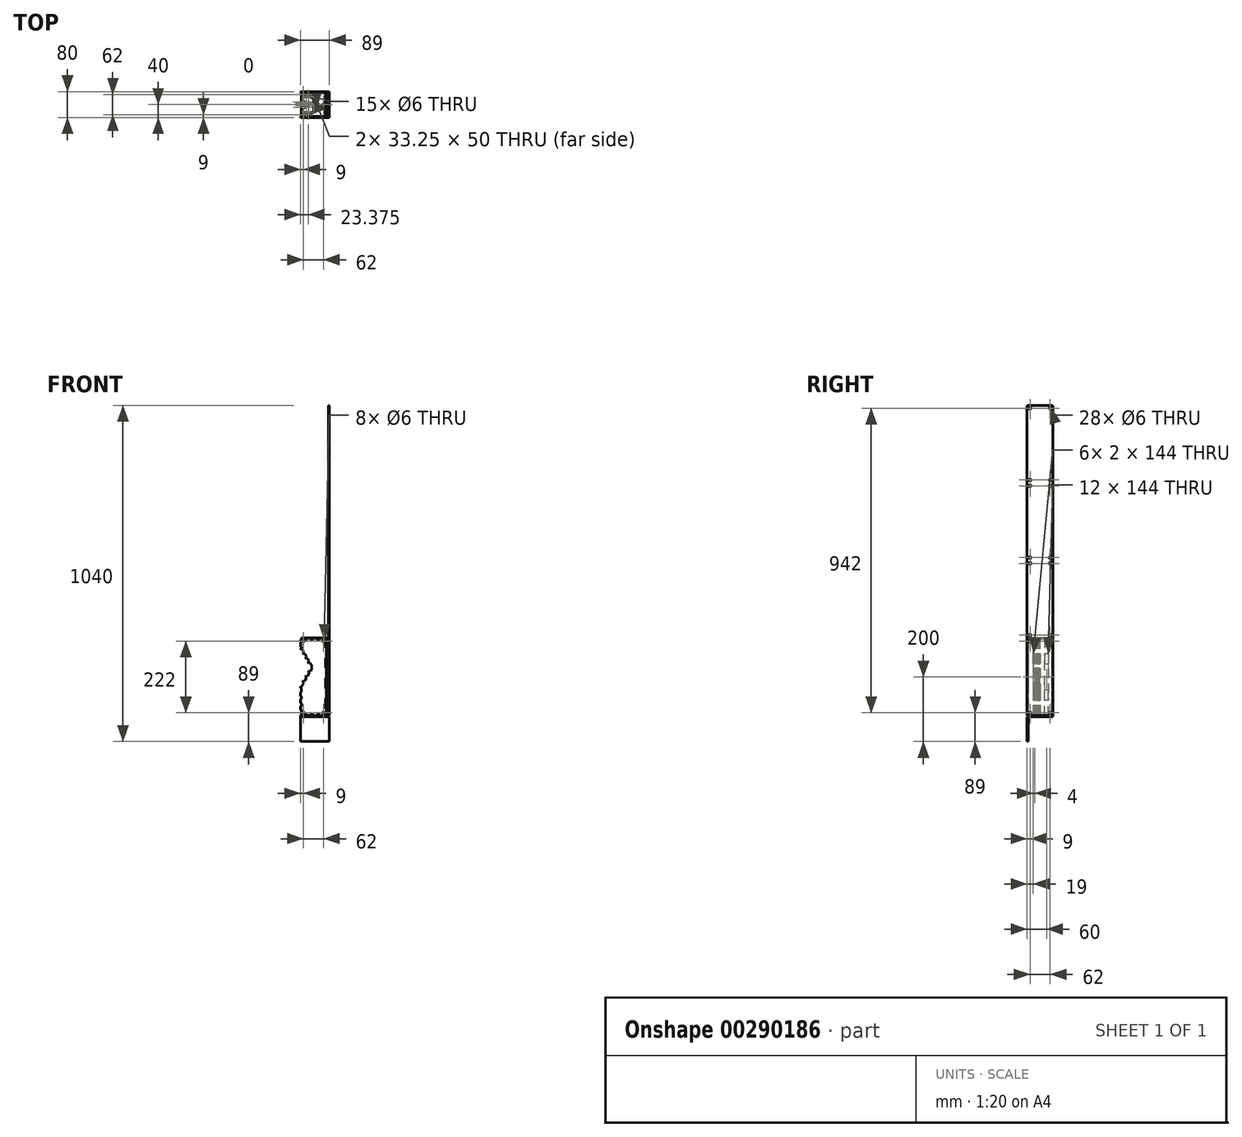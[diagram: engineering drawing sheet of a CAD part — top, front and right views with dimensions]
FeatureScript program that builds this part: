
annotation { "Feature Type Name" : "Feature", "Feature Type Description" : "" }
export const myFeature = defineFeature(function(context is Context, id is Id, definition is map)
    precondition{}
    {
        {
            assignVariable(context, id + "F0", {"name" : "WT", "anyValue" : 3});
        }
        {
            assignVariable(context, id + "F1", {"name" : "HD", "anyValue" : 3});
        }
        {
            var Q0;
            Q0=qCreatedBy(makeId("Front.planeOp"),FACE);
            var sketch = newSketch(context, id + "F2", { "sketchPlane" : qUnion([Q0])});
            skLineSegment(sketch, "E0", {"start": v(0, 0) * mm, "end": v(0, 240) * mm});
            skLineSegment(sketch, "E1", {"start": v(0, 120) * mm, "end": v(-80, 120) * mm, "construction": true});
            skLineSegment(sketch, "E2", {"start": v(0, 0) * mm, "end": v(-80, 0) * mm});
            skLineSegment(sketch, "E3", {"start": v(-80, 0) * mm, "end": v(-80, 90.56) * mm});
            skLineSegment(sketch, "E4", {"start": v(-80, 90.56) * mm, "end": v(-46, 149.44) * mm});
            skLineSegment(sketch, "E5", {"start": v(-46, 149.44) * mm, "end": v(-80, 208.33) * mm});
            skLineSegment(sketch, "E6", {"start": v(-80, 208.33) * mm, "end": v(-80, 240) * mm});
            skLineSegment(sketch, "E7", {"start": v(-80, 240) * mm, "end": v(0, 240) * mm});
            skLineSegment(sketch, "E8", {"start": v(-80, 90.56) * mm, "end": v(0, 90.56) * mm, "construction": true});
            skLineSegment(sketch, "E9", {"start": v(-80, 208.33) * mm, "end": v(0, 208.33) * mm, "construction": true});
            skPoint(sketch, "E10", {"position": v(-63, 120) * mm});
            skLineSegment(sketch, "E11", {"start": v(-80, 90.56) * mm, "end": v(-77, 90.56) * mm});
            skLineSegment(sketch, "E12", {"start": v(-77, 90.56) * mm, "end": v(-77, 0) * mm});
            skLineSegment(sketch, "E13", {"start": v(-3, 0) * mm, "end": v(-3, 240) * mm});
            skLineSegment(sketch, "E14", {"start": v(0, 237) * mm, "end": v(-80, 237) * mm});
            skLineSegment(sketch, "E15", {"start": v(-77, 240) * mm, "end": v(-77, 208.33) * mm});
            skLineSegment(sketch, "E16", {"start": v(-80, 208.33) * mm, "end": v(-77, 208.33) * mm});
            skLineSegment(sketch, "E17", {"start": v(-80, 3) * mm, "end": v(0, 3) * mm});
            skLineSegment(sketch, "E18", {"start": v(-80, 90.56) * mm, "end": v(-77.4, 89.06) * mm});
            skLineSegment(sketch, "E19", {"start": v(-77.4, 89.06) * mm, "end": v(-43.4, 147.94) * mm});
            skLineSegment(sketch, "E20", {"start": v(-80, 208.33) * mm, "end": v(-77.4, 209.83) * mm});
            skLineSegment(sketch, "E21", {"start": v(-77.4, 209.83) * mm, "end": v(-42.54, 149.44) * mm});
            skLineSegment(sketch, "E22", {"start": v(-46, 149.44) * mm, "end": v(-45.13, 147.94) * mm});
            skLineSegment(sketch, "E23", {"start": v(-45.13, 147.94) * mm, "end": v(-42.54, 149.44) * mm});
            skLineSegment(sketch, "E24", {"start": v(-43.4, 147.94) * mm, "end": v(-42.54, 149.44) * mm});
            skLineSegment(sketch, "E25", {"start": v(-46, 149.44) * mm, "end": v(-45.13, 150.94) * mm});
            skLineSegment(sketch, "E26", {"start": v(-45.13, 150.94) * mm, "end": v(-42.54, 149.44) * mm});
            skLineSegment(sketch, "E27", {"start": v(-76.65, 208.54) * mm, "end": v(-79.25, 207.04) * mm});
            skLineSegment(sketch, "E28", {"start": v(-46.43, 150.2) * mm, "end": v(-43.83, 151.7) * mm});
            skPoint(sketch, "E29", {"position": v(-79.25, 207.04) * mm});
            skPoint(sketch, "E30", {"position": v(-46.43, 150.2) * mm});
            skPoint(sketch, "E31", {"position": v(-80, 89.06) * mm});
            skCircle(sketch, "E32", {"center": v(-71, 231) * mm, "radius": 3 * mm});
            skLineSegment(sketch, "E33", {"start": v(-40, 208.33) * mm, "end": v(-40, 225.54) * mm, "construction": true});
            skCircle(sketch, "E34.MirrorC", {"center": v(-9, 231) * mm, "radius": 3 * mm});
            skCircle(sketch, "E35.MirrorC", {"center": v(-71, 9) * mm, "radius": 3 * mm});
            skCircle(sketch, "E36.MirrorC", {"center": v(-9, 9) * mm, "radius": 3 * mm});
            skSolve(sketch);
        }
        {
            var Q0;
            Q0=qCreatedBy(makeId("Front.planeOp"),FACE);
            var sketch = newSketch(context, id + "F3", { "sketchPlane" : qUnion([Q0])});
            skLineSegment(sketch, "E37.0", {"start": v(-80, 240) * mm, "end": v(0, 240) * mm});
            skLineSegment(sketch, "E37.1", {"start": v(-80, 208.33) * mm, "end": v(-80, 240) * mm});
            skLineSegment(sketch, "E37.2", {"start": v(-46, 149.44) * mm, "end": v(-80, 208.33) * mm});
            skLineSegment(sketch, "E37.3", {"start": v(-80, 90.56) * mm, "end": v(-46, 149.44) * mm});
            skLineSegment(sketch, "E37.4", {"start": v(-80, 0) * mm, "end": v(-80, 90.56) * mm});
            skLineSegment(sketch, "E37.5", {"start": v(0, 0) * mm, "end": v(-80, 0) * mm});
            skLineSegment(sketch, "E37.6", {"start": v(0, 0) * mm, "end": v(0, 240) * mm});
            skCircle(sketch, "E38.0", {"center": v(-71, 231) * mm, "radius": 3 * mm});
            skCircle(sketch, "E38.1", {"center": v(-9, 231) * mm, "radius": 3 * mm});
            skCircle(sketch, "E38.2", {"center": v(-71, 9) * mm, "radius": 3 * mm});
            skCircle(sketch, "E38.3", {"center": v(-9, 9) * mm, "radius": 3 * mm});
            skLineSegment(sketch, "E39", {"start": v(0, -80) * mm, "end": v(-80, -80) * mm});
            skLineSegment(sketch, "E40", {"start": v(-80, -80) * mm, "end": v(-80, 0) * mm});
            skLineSegment(sketch, "E41", {"start": v(0, 0) * mm, "end": v(9, 0) * mm});
            skLineSegment(sketch, "E42", {"start": v(9, 0) * mm, "end": v(9, -80) * mm});
            skLineSegment(sketch, "E43", {"start": v(9, -80) * mm, "end": v(0, -80) * mm});
            skSolve(sketch);
        }
        {
            var Q0;
            Q0=sQuery(id+"F2.wireOp",EDGE,"E7");
            cPlane(context, id + "F4", {"entities" : qUnion([Q0]), "cplaneType" : CPlaneType.LINE_ANGLE, "offset" : 25 * mm, "angle" : 90 * degree, "width" : 150 * mm, "height" : 150 * mm});
        }
        {
            var Q0;
            Q0=qCreatedBy(id+"F4.planeOp",FACE);
            var sketch = newSketch(context, id + "F5", { "sketchPlane" : qUnion([Q0])});
            skLineSegment(sketch, "E44.0", {"start": v(-80, 0) * mm, "end": v(0, 0) * mm});
            skLineSegment(sketch, "E45", {"start": v(-80, 0) * mm, "end": v(-80, 80) * mm});
            skLineSegment(sketch, "E46", {"start": v(-80, 80) * mm, "end": v(0, 80) * mm});
            skLineSegment(sketch, "E47", {"start": v(0, 80) * mm, "end": v(0, 0) * mm});
            skLineSegment(sketch, "E48", {"start": v(0, 40) * mm, "end": v(-80, 40) * mm, "construction": true});
            skLineSegment(sketch, "E49", {"start": v(-80, 77) * mm, "end": v(0, 77) * mm});
            skLineSegment(sketch, "E50", {"start": v(-70, 80) * mm, "end": v(-70, 77) * mm});
            skLineSegment(sketch, "E51.1.0.0", {"start": v(-60, 80) * mm, "end": v(-60, 77) * mm});
            skLineSegment(sketch, "E51.2.0.0", {"start": v(-50, 80) * mm, "end": v(-50, 77) * mm});
            skLineSegment(sketch, "E51.3.0.0", {"start": v(-40, 80) * mm, "end": v(-40, 77) * mm});
            skLineSegment(sketch, "E51.4.0.0", {"start": v(-30, 80) * mm, "end": v(-30, 77) * mm});
            skLineSegment(sketch, "E51.5.0.0", {"start": v(-20, 80) * mm, "end": v(-20, 77) * mm});
            skLineSegment(sketch, "E51.6.0.0", {"start": v(-10, 80) * mm, "end": v(-10, 77) * mm});
            skLineSegment(sketch, "E51.direction1", {"start": v(-70, 77) * mm, "end": v(-60, 77) * mm, "construction": true});
            skLineSegment(sketch, "E52.MirrorCS", {"start": v(-80, 3) * mm, "end": v(0, 3) * mm});
            skLineSegment(sketch, "E53.MirrorCS", {"start": v(-70, 0) * mm, "end": v(-70, 3) * mm});
            skLineSegment(sketch, "E54.MirrorCS", {"start": v(-60, 0) * mm, "end": v(-60, 3) * mm});
            skLineSegment(sketch, "E55.MirrorCS", {"start": v(-50, 0) * mm, "end": v(-50, 3) * mm});
            skLineSegment(sketch, "E56.MirrorCS", {"start": v(-40, 0) * mm, "end": v(-40, 3) * mm});
            skLineSegment(sketch, "E57.MirrorCS", {"start": v(-30, 0) * mm, "end": v(-30, 3) * mm});
            skLineSegment(sketch, "E58.MirrorCS", {"start": v(-20, 0) * mm, "end": v(-20, 3) * mm});
            skLineSegment(sketch, "E59.MirrorCS", {"start": v(-10, 0) * mm, "end": v(-10, 3) * mm});
            skLineSegment(sketch, "E60", {"start": v(-77, 80) * mm, "end": v(-77, 0) * mm});
            skLineSegment(sketch, "E61", {"start": v(-80, 71.1) * mm, "end": v(-77, 71.1) * mm});
            skLineSegment(sketch, "E62.0.1.0", {"start": v(-80, 62.34) * mm, "end": v(-77, 62.34) * mm});
            skLineSegment(sketch, "E62.0.2.0", {"start": v(-80, 53.6) * mm, "end": v(-77, 53.6) * mm});
            skLineSegment(sketch, "E62.0.3.0", {"start": v(-80, 44.84) * mm, "end": v(-77, 44.84) * mm});
            skLineSegment(sketch, "E62.0.4.0", {"start": v(-80, 36.1) * mm, "end": v(-77, 36.1) * mm});
            skLineSegment(sketch, "E62.0.5.0", {"start": v(-80, 27.34) * mm, "end": v(-77, 27.34) * mm});
            skLineSegment(sketch, "E62.0.6.0", {"start": v(-80, 18.6) * mm, "end": v(-77, 18.6) * mm});
            skLineSegment(sketch, "E62.direction1", {"start": v(-86.03, 71.1) * mm, "end": v(-80, 71.1) * mm, "construction": true});
            skLineSegment(sketch, "E62.direction2", {"start": v(-80, 71.1) * mm, "end": v(-80, 62.34) * mm, "construction": true});
            skLineSegment(sketch, "E63", {"start": v(-40, 40) * mm, "end": v(-40, 50.28) * mm, "construction": true});
            skLineSegment(sketch, "E64.MirrorCS", {"start": v(0, 18.6) * mm, "end": v(-3, 18.6) * mm});
            skLineSegment(sketch, "E65.MirrorCS", {"start": v(0, 27.34) * mm, "end": v(-3, 27.34) * mm});
            skLineSegment(sketch, "E66.MirrorCS", {"start": v(0, 36.1) * mm, "end": v(-3, 36.1) * mm});
            skLineSegment(sketch, "E67.MirrorCS", {"start": v(0, 44.84) * mm, "end": v(-3, 44.84) * mm});
            skLineSegment(sketch, "E68.MirrorCS", {"start": v(0, 53.6) * mm, "end": v(-3, 53.6) * mm});
            skLineSegment(sketch, "E69.MirrorCS", {"start": v(0, 62.34) * mm, "end": v(-3, 62.34) * mm});
            skLineSegment(sketch, "E70.MirrorCS", {"start": v(0, 71.1) * mm, "end": v(-3, 71.1) * mm});
            skLineSegment(sketch, "E71.MirrorCS", {"start": v(-3, 80) * mm, "end": v(-3, 0) * mm});
            skLineSegment(sketch, "E72.bottom", {"start": v(-40, 15) * mm, "end": v(-73.25, 15) * mm});
            skLineSegment(sketch, "E72.top", {"start": v(-40, 65) * mm, "end": v(-73.25, 65) * mm});
            skLineSegment(sketch, "E72.left", {"start": v(-6.75, 40) * mm, "end": v(-6.75, 65) * mm, "construction": true});
            skLineSegment(sketch, "E72.right", {"start": v(-73.25, 15) * mm, "end": v(-73.25, 65) * mm});
            skPoint(sketch, "E72.middle", {"position": v(-40, 40) * mm});
            skCircle(sketch, "E73", {"center": v(-9, 40) * mm, "radius": 3 * mm});
            skCircle(sketch, "E74.MirrorC", {"center": v(-71, 71) * mm, "radius": 3 * mm});
            skLineSegment(sketch, "E75", {"start": v(-40, 15) * mm, "end": v(-40, 65) * mm});
            skPoint(sketch, "E76.orphan", {"position": v(-6.75, 15) * mm});
            skCircle(sketch, "E77.MirrorC", {"center": v(-71, 9) * mm, "radius": 3 * mm});
            skLineSegment(sketch, "E78.0.0.7", {"start": v(-80, 9.84) * mm, "end": v(-77, 9.84) * mm});
            skLineSegment(sketch, "E79.MirrorCS", {"start": v(0, 9.84) * mm, "end": v(-3, 9.84) * mm});
            skSolve(sketch);
        }
        {
            var Q0;
            Q0=sQuery(id+"F2.wireOp",EDGE,"E0");
            cPlane(context, id + "F6", {"entities" : qUnion([Q0]), "cplaneType" : CPlaneType.LINE_ANGLE, "offset" : 25 * mm, "angle" : 0 * degree, "width" : 150 * mm, "height" : 150 * mm});
        }
        {
            var Q0;
            Q0=qCreatedBy(id+"F6.planeOp",FACE);
            var sketch = newSketch(context, id + "F7", { "sketchPlane" : qUnion([Q0])});
            skLineSegment(sketch, "E80.0", {"start": v(0, 0) * mm, "end": v(0, 240) * mm});
            skLineSegment(sketch, "E81.0", {"start": v(80, 240) * mm, "end": v(0, 240) * mm});
            skLineSegment(sketch, "E82", {"start": v(80, 240) * mm, "end": v(80, 0) * mm});
            skLineSegment(sketch, "E83", {"start": v(80, 0) * mm, "end": v(0, 0) * mm});
            skLineSegment(sketch, "E84", {"start": v(3, 240) * mm, "end": v(3, 0) * mm});
            skLineSegment(sketch, "E85", {"start": v(0, 210) * mm, "end": v(3, 210) * mm});
            skLineSegment(sketch, "E86.0.1.0", {"start": v(0, 178.75) * mm, "end": v(3, 178.75) * mm});
            skLineSegment(sketch, "E86.0.2.0", {"start": v(0, 147.5) * mm, "end": v(3, 147.5) * mm});
            skLineSegment(sketch, "E86.0.3.0", {"start": v(0, 116.25) * mm, "end": v(3, 116.25) * mm});
            skLineSegment(sketch, "E86.0.4.0", {"start": v(0, 85) * mm, "end": v(3, 85) * mm});
            skLineSegment(sketch, "E86.0.5.0", {"start": v(0, 53.75) * mm, "end": v(3, 53.75) * mm});
            skLineSegment(sketch, "E86.0.6.0", {"start": v(0, 22.5) * mm, "end": v(3, 22.5) * mm});
            skLineSegment(sketch, "E86.direction1", {"start": v(-5.68, 210) * mm, "end": v(0, 210) * mm, "construction": true});
            skLineSegment(sketch, "E86.direction2", {"start": v(0, 210) * mm, "end": v(0, 178.75) * mm, "construction": true});
            skLineSegment(sketch, "E87", {"start": v(40, 240) * mm, "end": v(40, 220.49) * mm, "construction": true});
            skPoint(sketch, "E87.endSnap0", {"position": v(40, 240) * mm});
            skLineSegment(sketch, "E88.MirrorCS", {"start": v(77, 240) * mm, "end": v(77, 0) * mm});
            skLineSegment(sketch, "E89.MirrorCS", {"start": v(80, 210) * mm, "end": v(77, 210) * mm});
            skLineSegment(sketch, "E90.MirrorCS", {"start": v(80, 178.75) * mm, "end": v(77, 178.75) * mm});
            skLineSegment(sketch, "E91.MirrorCS", {"start": v(80, 147.5) * mm, "end": v(77, 147.5) * mm});
            skLineSegment(sketch, "E92.MirrorCS", {"start": v(80, 116.25) * mm, "end": v(77, 116.25) * mm});
            skLineSegment(sketch, "E93.MirrorCS", {"start": v(80, 85) * mm, "end": v(77, 85) * mm});
            skLineSegment(sketch, "E94.MirrorCS", {"start": v(80, 53.75) * mm, "end": v(77, 53.75) * mm});
            skLineSegment(sketch, "E95.MirrorCS", {"start": v(80, 22.5) * mm, "end": v(77, 22.5) * mm});
            skCircle(sketch, "E96", {"center": v(9, 231) * mm, "radius": 3 * mm});
            skCircle(sketch, "E97.MirrorC", {"center": v(71, 231) * mm, "radius": 3 * mm});
            skLineSegment(sketch, "E98", {"start": v(77, 120) * mm, "end": v(3, 120) * mm, "construction": true});
            skCircle(sketch, "E99.MirrorC", {"center": v(9, 9) * mm, "radius": 3 * mm});
            skCircle(sketch, "E100.MirrorC", {"center": v(71, 9) * mm, "radius": 3 * mm});
            skSolve(sketch);
        }
        {
            var Q0;
            Q0=sQuery(id+"F2.wireOp",EDGE,"E2");
            cPlane(context, id + "F8", {"entities" : qUnion([Q0]), "cplaneType" : CPlaneType.LINE_ANGLE, "offset" : 25 * mm, "angle" : 90 * degree, "width" : 150 * mm, "height" : 150 * mm});
        }
        {
            var Q0;
            Q0=qCreatedBy(id+"F8.planeOp",FACE);
            var sketch = newSketch(context, id + "F9", { "sketchPlane" : qUnion([Q0])});
            skLineSegment(sketch, "E101.0", {"start": v(-80, 0) * mm, "end": v(0, 0) * mm});
            skLineSegment(sketch, "E101.1", {"start": v(0, 80) * mm, "end": v(0, 0) * mm});
            skLineSegment(sketch, "E101.2", {"start": v(-80, 0) * mm, "end": v(-80, 80) * mm});
            skLineSegment(sketch, "E101.3", {"start": v(-80, 80) * mm, "end": v(0, 80) * mm});
            skLineSegment(sketch, "E101.4", {"start": v(-80, 77) * mm, "end": v(0, 77) * mm});
            skLineSegment(sketch, "E101.5", {"start": v(-3, 80) * mm, "end": v(-3, 0) * mm});
            skLineSegment(sketch, "E101.6", {"start": v(-77, 80) * mm, "end": v(-77, 0) * mm});
            skLineSegment(sketch, "E101.7", {"start": v(-70, 80) * mm, "end": v(-70, 77) * mm});
            skLineSegment(sketch, "E101.8", {"start": v(-60, 80) * mm, "end": v(-60, 77) * mm});
            skLineSegment(sketch, "E101.9", {"start": v(-50, 80) * mm, "end": v(-50, 77) * mm});
            skLineSegment(sketch, "E101.10", {"start": v(-40, 80) * mm, "end": v(-40, 77) * mm});
            skLineSegment(sketch, "E101.11", {"start": v(-30, 80) * mm, "end": v(-30, 77) * mm});
            skLineSegment(sketch, "E101.12", {"start": v(-20, 80) * mm, "end": v(-20, 77) * mm});
            skLineSegment(sketch, "E101.13", {"start": v(-10, 80) * mm, "end": v(-10, 77) * mm});
            skLineSegment(sketch, "E101.14", {"start": v(0, 71.1) * mm, "end": v(-3, 71.1) * mm});
            skLineSegment(sketch, "E101.15", {"start": v(0, 62.34) * mm, "end": v(-3, 62.34) * mm});
            skLineSegment(sketch, "E101.16", {"start": v(0, 53.6) * mm, "end": v(-3, 53.6) * mm});
            skLineSegment(sketch, "E101.17", {"start": v(0, 36.1) * mm, "end": v(-3, 36.1) * mm});
            skLineSegment(sketch, "E101.18", {"start": v(0, 27.34) * mm, "end": v(-3, 27.34) * mm});
            skLineSegment(sketch, "E101.19", {"start": v(0, 18.6) * mm, "end": v(-3, 18.6) * mm});
            skLineSegment(sketch, "E101.20", {"start": v(-80, 3) * mm, "end": v(0, 3) * mm});
            skLineSegment(sketch, "E101.21", {"start": v(-10, 0) * mm, "end": v(-10, 3) * mm});
            skLineSegment(sketch, "E101.22", {"start": v(-20, 0) * mm, "end": v(-20, 3) * mm});
            skLineSegment(sketch, "E101.23", {"start": v(-30, 0) * mm, "end": v(-30, 3) * mm});
            skLineSegment(sketch, "E101.24", {"start": v(-40, 0) * mm, "end": v(-40, 3) * mm});
            skLineSegment(sketch, "E101.25", {"start": v(-50, 0) * mm, "end": v(-50, 3) * mm});
            skLineSegment(sketch, "E101.26", {"start": v(-60, 0) * mm, "end": v(-60, 3) * mm});
            skLineSegment(sketch, "E101.27", {"start": v(-70, 0) * mm, "end": v(-70, 3) * mm});
            skLineSegment(sketch, "E101.28", {"start": v(-80, 18.6) * mm, "end": v(-77, 18.6) * mm});
            skLineSegment(sketch, "E101.29", {"start": v(-80, 27.34) * mm, "end": v(-77, 27.34) * mm});
            skLineSegment(sketch, "E101.30", {"start": v(-80, 36.1) * mm, "end": v(-77, 36.1) * mm});
            skLineSegment(sketch, "E101.31", {"start": v(-80, 44.84) * mm, "end": v(-77, 44.84) * mm});
            skLineSegment(sketch, "E101.32", {"start": v(-80, 53.6) * mm, "end": v(-77, 53.6) * mm});
            skLineSegment(sketch, "E101.33", {"start": v(-80, 62.34) * mm, "end": v(-77, 62.34) * mm});
            skLineSegment(sketch, "E101.34", {"start": v(-80, 71.1) * mm, "end": v(-77, 71.1) * mm});
            skLineSegment(sketch, "E101.35", {"start": v(0, 44.84) * mm, "end": v(-3, 44.84) * mm});
            skCircle(sketch, "E102.0", {"center": v(-71, 71) * mm, "radius": 3 * mm});
            skCircle(sketch, "E102.2", {"center": v(-9, 40) * mm, "radius": 3 * mm});
            skLineSegment(sketch, "E103.0", {"start": v(-6.75, 40) * mm, "end": v(-6.75, 65) * mm});
            skLineSegment(sketch, "E104", {"start": v(-6.75, 52.5) * mm, "end": v(-34.86, 52.5) * mm, "construction": true});
            skLineSegment(sketch, "E105.0", {"start": v(-73.25, 15) * mm, "end": v(-73.25, 65) * mm});
            skLineSegment(sketch, "E106", {"start": v(-73.25, 40) * mm, "end": v(-49.8, 40) * mm, "construction": true});
            skPoint(sketch, "E106.endSnap0", {"position": v(-73.25, 40) * mm});
            skCircle(sketch, "E107", {"center": v(-70.25, 40) * mm, "radius": 3 * mm});
            skLineSegment(sketch, "E108", {"start": v(-70.25, 40) * mm, "end": v(-70.25, 48) * mm, "construction": true});
            skCircle(sketch, "E109", {"center": v(-70.25, 48) * mm, "radius": 3 * mm});
            skCircle(sketch, "E110.MirrorC", {"center": v(-70.25, 32) * mm, "radius": 3 * mm});
            skLineSegment(sketch, "E111", {"start": v(-70.25, 44) * mm, "end": v(-62.25, 44) * mm, "construction": true});
            skCircle(sketch, "E112", {"center": v(-62.25, 44) * mm, "radius": 3 * mm});
            skCircle(sketch, "E113.MirrorC", {"center": v(-62.25, 36) * mm, "radius": 3 * mm});
            skLineSegment(sketch, "E114", {"start": v(-62.25, 44) * mm, "end": v(-62.25, 31.93) * mm, "construction": true});
            skCircle(sketch, "E115.MirrorC", {"center": v(-54.25, 40) * mm, "radius": 3 * mm});
            skCircle(sketch, "E116.0", {"center": v(-71, 9) * mm, "radius": 3 * mm});
            skSolve(sketch);
        }
        {
            var Q0;
            Q0=sQuery(id+"F7.wireOp",EDGE,"E82");
            cPlane(context, id + "F10", {"entities" : qUnion([Q0]), "cplaneType" : CPlaneType.LINE_ANGLE, "offset" : 25 * mm, "angle" : 90 * degree, "width" : 150 * mm, "height" : 150 * mm});
        }
        {
            var Q0;
            Q0=qCreatedBy(id+"F10.planeOp",FACE);
            var sketch = newSketch(context, id + "F11", { "sketchPlane" : qUnion([Q0])});
            skLineSegment(sketch, "E117.0", {"start": v(80, 208.33) * mm, "end": v(80, 240) * mm});
            skLineSegment(sketch, "E117.1", {"start": v(46, 149.44) * mm, "end": v(80, 208.33) * mm});
            skLineSegment(sketch, "E117.2", {"start": v(80, 90.56) * mm, "end": v(46, 149.44) * mm});
            skLineSegment(sketch, "E117.3", {"start": v(80, 0) * mm, "end": v(80, 90.56) * mm});
            skLineSegment(sketch, "E117.4", {"start": v(0, 0) * mm, "end": v(80, 0) * mm});
            skLineSegment(sketch, "E117.5", {"start": v(0, 0) * mm, "end": v(0, 240) * mm});
            skLineSegment(sketch, "E117.6", {"start": v(80, 240) * mm, "end": v(0, 240) * mm});
            skCircle(sketch, "E118", {"center": v(9, 231) * mm, "radius": 3 * mm});
            skLineSegment(sketch, "E119", {"start": v(40, 240) * mm, "end": v(40, 223.94) * mm, "construction": true});
            skCircle(sketch, "E120.MirrorC", {"center": v(71, 231) * mm, "radius": 3 * mm});
            skCircle(sketch, "E121.MirrorC", {"center": v(9, 9) * mm, "radius": 3 * mm});
            skCircle(sketch, "E122.MirrorC", {"center": v(71, 9) * mm, "radius": 3 * mm});
            skSolve(sketch);
        }
        {
            var Q0;
            Q0=sQuery(id+"F2.wireOp",EDGE,"E6");
            cPlane(context, id + "F12", {"entities" : qUnion([Q0]), "cplaneType" : CPlaneType.LINE_ANGLE, "offset" : 25 * mm, "angle" : 0 * degree, "width" : 150 * mm, "height" : 150 * mm});
        }
        {
            var Q0;
            Q0=qCreatedBy(id+"F12.planeOp",FACE);
            var sketch = newSketch(context, id + "F13", { "sketchPlane" : qUnion([Q0])});
            skLineSegment(sketch, "E123.0", {"start": v(0, 208.33) * mm, "end": v(0, 240) * mm});
            skLineSegment(sketch, "E124.0", {"start": v(0, 240) * mm, "end": v(80, 240) * mm});
            skLineSegment(sketch, "E125", {"start": v(80, 240) * mm, "end": v(80, 208.33) * mm});
            skLineSegment(sketch, "E126", {"start": v(80, 208.33) * mm, "end": v(0, 208.33) * mm});
            skLineSegment(sketch, "E127", {"start": v(80, 224.17) * mm, "end": v(0, 224.17) * mm, "construction": true});
            skLineSegment(sketch, "E128", {"start": v(80, 226.57) * mm, "end": v(77, 226.57) * mm});
            skLineSegment(sketch, "E129", {"start": v(77, 226.57) * mm, "end": v(77, 224.17) * mm});
            skLineSegment(sketch, "E130.MirrorCS", {"start": v(77, 221.77) * mm, "end": v(77, 224.17) * mm});
            skLineSegment(sketch, "E131.MirrorCS", {"start": v(80, 221.77) * mm, "end": v(77, 221.77) * mm});
            skLineSegment(sketch, "E132", {"start": v(80, 240) * mm, "end": v(0, 224.17) * mm, "construction": true});
            skLineSegment(sketch, "E133", {"start": v(40, 232.08) * mm, "end": v(80, 232.08) * mm, "construction": true});
            skLineSegment(sketch, "E134", {"start": v(80, 234.48) * mm, "end": v(77, 234.48) * mm});
            skLineSegment(sketch, "E135", {"start": v(77, 234.48) * mm, "end": v(77, 232.08) * mm});
            skLineSegment(sketch, "E136.MirrorCS", {"start": v(77, 229.68) * mm, "end": v(77, 232.08) * mm});
            skLineSegment(sketch, "E137.MirrorCS", {"start": v(80, 229.68) * mm, "end": v(77, 229.68) * mm});
            skLineSegment(sketch, "E138.MirrorCS", {"start": v(80, 218.65) * mm, "end": v(77, 218.65) * mm});
            skLineSegment(sketch, "E139.MirrorCS", {"start": v(77, 218.65) * mm, "end": v(77, 216.25) * mm});
            skLineSegment(sketch, "E140.MirrorCS", {"start": v(77, 213.85) * mm, "end": v(77, 216.25) * mm});
            skLineSegment(sketch, "E141.MirrorCS", {"start": v(80, 213.85) * mm, "end": v(77, 213.85) * mm});
            skLineSegment(sketch, "E142", {"start": v(40, 224.17) * mm, "end": v(40, 240) * mm, "construction": true});
            skLineSegment(sketch, "E143.MirrorCS", {"start": v(0, 234.48) * mm, "end": v(3, 234.48) * mm});
            skLineSegment(sketch, "E144.MirrorCS", {"start": v(3, 234.48) * mm, "end": v(3, 232.08) * mm});
            skLineSegment(sketch, "E145.MirrorCS", {"start": v(3, 229.68) * mm, "end": v(3, 232.08) * mm});
            skLineSegment(sketch, "E146.MirrorCS", {"start": v(0, 229.68) * mm, "end": v(3, 229.68) * mm});
            skLineSegment(sketch, "E147.MirrorCS", {"start": v(0, 226.57) * mm, "end": v(3, 226.57) * mm});
            skLineSegment(sketch, "E148.MirrorCS", {"start": v(3, 226.57) * mm, "end": v(3, 224.17) * mm});
            skLineSegment(sketch, "E149.MirrorCS", {"start": v(3, 221.77) * mm, "end": v(3, 224.17) * mm});
            skLineSegment(sketch, "E150.MirrorCS", {"start": v(0, 221.77) * mm, "end": v(3, 221.77) * mm});
            skLineSegment(sketch, "E151.MirrorCS", {"start": v(0, 218.65) * mm, "end": v(3, 218.65) * mm});
            skLineSegment(sketch, "E152.MirrorCS", {"start": v(3, 218.65) * mm, "end": v(3, 216.25) * mm});
            skLineSegment(sketch, "E153.MirrorCS", {"start": v(3, 213.85) * mm, "end": v(3, 216.25) * mm});
            skLineSegment(sketch, "E154.MirrorCS", {"start": v(0, 213.85) * mm, "end": v(3, 213.85) * mm});
            skSolve(sketch);
        }
        {
            var Q0;
            Q0=sQuery(id+"F11.wireOp",EDGE,"E117.3");
            cPlane(context, id + "F14", {"entities" : qUnion([Q0]), "cplaneType" : CPlaneType.LINE_ANGLE, "offset" : 25 * mm, "angle" : 0 * degree, "width" : 150 * mm, "height" : 150 * mm});
        }
        {
            var Q0;
            Q0=qCreatedBy(id+"F14.planeOp",FACE);
            var sketch = newSketch(context, id + "F15", { "sketchPlane" : qUnion([Q0])});
            skLineSegment(sketch, "E155.0", {"start": v(80, 0) * mm, "end": v(80, 90.56) * mm});
            skLineSegment(sketch, "E156.0", {"start": v(0, 0) * mm, "end": v(80, 0) * mm});
            skLineSegment(sketch, "E157", {"start": v(80, 89.06) * mm, "end": v(0, 89.06) * mm});
            skLineSegment(sketch, "E158", {"start": v(0, 89.06) * mm, "end": v(0, 0) * mm});
            skLineSegment(sketch, "E159", {"start": v(80, 45.28) * mm, "end": v(0, 44.53) * mm, "construction": true});
            skLineSegment(sketch, "E160", {"start": v(0, 44.53) * mm, "end": v(80, 89.06) * mm, "construction": true});
            skLineSegment(sketch, "E161", {"start": v(80, 51.28) * mm, "end": v(77, 51.25) * mm});
            skLineSegment(sketch, "E162", {"start": v(77, 51.25) * mm, "end": v(77, 45.25) * mm});
            skLineSegment(sketch, "E163.MirrorCS", {"start": v(77.11, 39.25) * mm, "end": v(77, 45.25) * mm});
            skLineSegment(sketch, "E164.MirrorCS", {"start": v(80.11, 39.28) * mm, "end": v(77.11, 39.25) * mm});
            skLineSegment(sketch, "E165", {"start": v(40, 66.8) * mm, "end": v(80, 66.8) * mm, "construction": true});
            skLineSegment(sketch, "E166", {"start": v(80, 72.8) * mm, "end": v(77, 72.8) * mm});
            skLineSegment(sketch, "E167", {"start": v(77, 72.8) * mm, "end": v(77, 66.8) * mm});
            skLineSegment(sketch, "E168.MirrorCS", {"start": v(77, 60.8) * mm, "end": v(77, 66.8) * mm});
            skLineSegment(sketch, "E169.MirrorCS", {"start": v(80, 60.8) * mm, "end": v(77, 60.8) * mm});
            skLineSegment(sketch, "E170.MirrorCS", {"start": v(80.3, 29.77) * mm, "end": v(77.3, 29.71) * mm});
            skLineSegment(sketch, "E171.MirrorCS", {"start": v(77.3, 29.71) * mm, "end": v(77.4, 23.71) * mm});
            skLineSegment(sketch, "E172.MirrorCS", {"start": v(77.52, 17.71) * mm, "end": v(77.4, 23.71) * mm});
            skLineSegment(sketch, "E173.MirrorCS", {"start": v(80.52, 17.77) * mm, "end": v(77.52, 17.71) * mm});
            skLineSegment(sketch, "E174", {"start": v(40, 66.8) * mm, "end": v(40, 35.43) * mm, "construction": true});
            skPoint(sketch, "E174.endSnap0", {"position": v(40, 44.9) * mm});
            skLineSegment(sketch, "E175.MirrorCS", {"start": v(0, 72.8) * mm, "end": v(3, 72.8) * mm});
            skLineSegment(sketch, "E176.MirrorCS", {"start": v(3, 72.8) * mm, "end": v(3, 66.8) * mm});
            skLineSegment(sketch, "E177.MirrorCS", {"start": v(3, 60.8) * mm, "end": v(3, 66.8) * mm});
            skLineSegment(sketch, "E178.MirrorCS", {"start": v(0, 60.8) * mm, "end": v(3, 60.8) * mm});
            skLineSegment(sketch, "E179.MirrorCS", {"start": v(0, 51.28) * mm, "end": v(3, 51.25) * mm});
            skLineSegment(sketch, "E180.MirrorCS", {"start": v(3, 51.25) * mm, "end": v(3, 45.25) * mm});
            skLineSegment(sketch, "E181.MirrorCS", {"start": v(2.89, 39.25) * mm, "end": v(3, 45.25) * mm});
            skLineSegment(sketch, "E182.MirrorCS", {"start": v(-0.11, 39.28) * mm, "end": v(2.89, 39.25) * mm});
            skLineSegment(sketch, "E183.MirrorCS", {"start": v(-0.3, 29.77) * mm, "end": v(2.7, 29.71) * mm});
            skLineSegment(sketch, "E184.MirrorCS", {"start": v(2.7, 29.71) * mm, "end": v(2.6, 23.71) * mm});
            skLineSegment(sketch, "E185.MirrorCS", {"start": v(2.48, 17.71) * mm, "end": v(2.6, 23.71) * mm});
            skLineSegment(sketch, "E186.MirrorCS", {"start": v(-0.52, 17.77) * mm, "end": v(2.48, 17.71) * mm});
            skPoint(sketch, "E187", {"position": v(80, 89.06) * mm});
            skLineSegment(sketch, "E188", {"start": v(0, 85.3) * mm, "end": v(3, 85.3) * mm});
            skLineSegment(sketch, "E189", {"start": v(3, 85.3) * mm, "end": v(3, 89.06) * mm});
            skLineSegment(sketch, "E190.MirrorCS", {"start": v(80, 85.3) * mm, "end": v(77, 85.3) * mm});
            skLineSegment(sketch, "E191.MirrorCS", {"start": v(77, 85.3) * mm, "end": v(77, 89.06) * mm});
            skSolve(sketch);
        }
        {
            var Q0;
            Q0=sQuery(id+"F2.wireOp",EDGE,"E5");
            cPlane(context, id + "F16", {"entities" : qUnion([Q0]), "cplaneType" : CPlaneType.LINE_ANGLE, "offset" : 25 * mm, "angle" : 0 * degree, "width" : 150 * mm, "height" : 150 * mm});
        }
        {
            var Q0;
            Q0=qCreatedBy(id+"F16.planeOp",FACE);
            var sketch = newSketch(context, id + "F17", { "sketchPlane" : qUnion([Q0])});
            skLineSegment(sketch, "E192.0", {"start": v(0, 152.42) * mm, "end": v(0, 220.42) * mm});
            skLineSegment(sketch, "E193", {"start": v(0, 153.29) * mm, "end": v(80, 153.29) * mm});
            skLineSegment(sketch, "E194", {"start": v(0, 218.92) * mm, "end": v(80, 218.92) * mm});
            skLineSegment(sketch, "E195", {"start": v(80, 218.92) * mm, "end": v(80, 153.29) * mm});
            skLineSegment(sketch, "E196", {"start": v(0, 186.42) * mm, "end": v(80, 186.42) * mm, "construction": true});
            skLineSegment(sketch, "E197", {"start": v(80, 186.42) * mm, "end": v(0, 218.92) * mm, "construction": true});
            skLineSegment(sketch, "E198", {"start": v(40, 202.67) * mm, "end": v(0, 202.67) * mm, "construction": true});
            skLineSegment(sketch, "E199", {"start": v(0, 190.17) * mm, "end": v(3, 190.17) * mm});
            skLineSegment(sketch, "E200", {"start": v(3, 190.17) * mm, "end": v(3, 186.42) * mm});
            skLineSegment(sketch, "E201.MirrorCS", {"start": v(3, 182.67) * mm, "end": v(3, 186.42) * mm});
            skLineSegment(sketch, "E202.MirrorCS", {"start": v(0, 182.67) * mm, "end": v(3, 182.67) * mm});
            skLineSegment(sketch, "E203", {"start": v(0, 206.42) * mm, "end": v(3, 206.42) * mm});
            skLineSegment(sketch, "E204", {"start": v(3, 206.42) * mm, "end": v(3, 202.67) * mm});
            skLineSegment(sketch, "E205.MirrorCS", {"start": v(3, 198.92) * mm, "end": v(3, 202.67) * mm});
            skLineSegment(sketch, "E206.MirrorCS", {"start": v(0, 198.92) * mm, "end": v(3, 198.92) * mm});
            skLineSegment(sketch, "E207.MirrorCS", {"start": v(3, 173.92) * mm, "end": v(3, 170.17) * mm});
            skLineSegment(sketch, "E208.MirrorCS", {"start": v(0, 173.92) * mm, "end": v(3, 173.92) * mm});
            skLineSegment(sketch, "E209.MirrorCS", {"start": v(3, 166.42) * mm, "end": v(3, 170.17) * mm});
            skLineSegment(sketch, "E210.MirrorCS", {"start": v(0, 166.42) * mm, "end": v(3, 166.42) * mm});
            skLineSegment(sketch, "E211", {"start": v(40, 202.67) * mm, "end": v(40, 174.67) * mm, "construction": true});
            skPoint(sketch, "E211.endSnap0", {"position": v(40, 186.42) * mm});
            skLineSegment(sketch, "E212.MirrorCS", {"start": v(80, 206.42) * mm, "end": v(77, 206.42) * mm});
            skLineSegment(sketch, "E213.MirrorCS", {"start": v(77, 206.42) * mm, "end": v(77, 202.67) * mm});
            skLineSegment(sketch, "E214.MirrorCS", {"start": v(77, 198.92) * mm, "end": v(77, 202.67) * mm});
            skLineSegment(sketch, "E215.MirrorCS", {"start": v(80, 198.92) * mm, "end": v(77, 198.92) * mm});
            skLineSegment(sketch, "E216.MirrorCS", {"start": v(80, 190.17) * mm, "end": v(77, 190.17) * mm});
            skLineSegment(sketch, "E217.MirrorCS", {"start": v(77, 190.17) * mm, "end": v(77, 186.42) * mm});
            skLineSegment(sketch, "E218.MirrorCS", {"start": v(77, 182.67) * mm, "end": v(77, 186.42) * mm});
            skLineSegment(sketch, "E219.MirrorCS", {"start": v(80, 182.67) * mm, "end": v(77, 182.67) * mm});
            skLineSegment(sketch, "E220.MirrorCS", {"start": v(80, 173.92) * mm, "end": v(77, 173.92) * mm});
            skLineSegment(sketch, "E221.MirrorCS", {"start": v(77, 173.92) * mm, "end": v(77, 170.17) * mm});
            skLineSegment(sketch, "E222.MirrorCS", {"start": v(77, 166.42) * mm, "end": v(77, 170.17) * mm});
            skLineSegment(sketch, "E223.MirrorCS", {"start": v(80, 166.42) * mm, "end": v(77, 166.42) * mm});
            skLineSegment(sketch, "E224", {"start": v(0, 215.17) * mm, "end": v(3, 215.17) * mm});
            skLineSegment(sketch, "E225", {"start": v(3, 215.17) * mm, "end": v(3, 218.92) * mm});
            skLineSegment(sketch, "E226.MirrorCS", {"start": v(77, 215.17) * mm, "end": v(77, 218.92) * mm});
            skLineSegment(sketch, "E227.MirrorCS", {"start": v(80, 215.17) * mm, "end": v(77, 215.17) * mm});
            skSolve(sketch);
        }
        {
            var Q0;
            Q0=sQuery(id+"F2.wireOp",EDGE,"E4");
            cPlane(context, id + "F18", {"entities" : qUnion([Q0]), "cplaneType" : CPlaneType.LINE_ANGLE, "offset" : 25 * mm, "angle" : 0 * degree, "width" : 150 * mm, "height" : 150 * mm});
        }
        {
            var Q0;
            Q0=qCreatedBy(id+"F18.planeOp",FACE);
            var sketch = newSketch(context, id + "F19", { "sketchPlane" : qUnion([Q0])});
            skLineSegment(sketch, "E228.0", {"start": v(0, 38.42) * mm, "end": v(0, 106.42) * mm});
            skLineSegment(sketch, "E228.1", {"start": v(0, 106.42) * mm, "end": v(0, 108.16) * mm});
            skLineSegment(sketch, "E229", {"start": v(0, 38.42) * mm, "end": v(80, 38.42) * mm});
            skLineSegment(sketch, "E230", {"start": v(80, 38.42) * mm, "end": v(80, 108.16) * mm});
            skLineSegment(sketch, "E231", {"start": v(80, 108.16) * mm, "end": v(0, 108.16) * mm});
            skLineSegment(sketch, "E232", {"start": v(80, 73.29) * mm, "end": v(0, 73.29) * mm, "construction": true});
            skLineSegment(sketch, "E233", {"start": v(0, 73.29) * mm, "end": v(80, 108.16) * mm, "construction": true});
            skLineSegment(sketch, "E234", {"start": v(40, 90.72) * mm, "end": v(0, 90.72) * mm, "construction": true});
            skLineSegment(sketch, "E235", {"start": v(0, 69.54) * mm, "end": v(3, 69.54) * mm});
            skLineSegment(sketch, "E236", {"start": v(3, 69.54) * mm, "end": v(3, 73.29) * mm});
            skLineSegment(sketch, "E237.MirrorCS", {"start": v(3, 77.04) * mm, "end": v(3, 73.29) * mm});
            skLineSegment(sketch, "E238.MirrorCS", {"start": v(0, 77.04) * mm, "end": v(3, 77.04) * mm});
            skLineSegment(sketch, "E239", {"start": v(0, 86.97) * mm, "end": v(3, 86.97) * mm});
            skPoint(sketch, "E239.endSnap0", {"position": v(3, 75.16) * mm});
            skLineSegment(sketch, "E240", {"start": v(3, 86.97) * mm, "end": v(3, 90.72) * mm});
            skLineSegment(sketch, "E241.MirrorCS", {"start": v(3, 94.47) * mm, "end": v(3, 90.72) * mm});
            skLineSegment(sketch, "E242.MirrorCS", {"start": v(0, 94.47) * mm, "end": v(3, 94.47) * mm});
            skLineSegment(sketch, "E243.MirrorCS", {"start": v(0, 59.6) * mm, "end": v(3, 59.6) * mm});
            skLineSegment(sketch, "E244.MirrorCS", {"start": v(3, 59.6) * mm, "end": v(3, 55.86) * mm});
            skLineSegment(sketch, "E245.MirrorCS", {"start": v(3, 52.1) * mm, "end": v(3, 55.86) * mm});
            skLineSegment(sketch, "E246.MirrorCS", {"start": v(0, 52.1) * mm, "end": v(3, 52.1) * mm});
            skLineSegment(sketch, "E247", {"start": v(40, 90.72) * mm, "end": v(40, 56.57) * mm, "construction": true});
            skLineSegment(sketch, "E248.MirrorCS", {"start": v(80, 52.1) * mm, "end": v(77, 52.1) * mm});
            skLineSegment(sketch, "E249.MirrorCS", {"start": v(77, 52.1) * mm, "end": v(77, 55.86) * mm});
            skLineSegment(sketch, "E250.MirrorCS", {"start": v(77, 59.6) * mm, "end": v(77, 55.86) * mm});
            skLineSegment(sketch, "E251.MirrorCS", {"start": v(80, 59.6) * mm, "end": v(77, 59.6) * mm});
            skLineSegment(sketch, "E252.MirrorCS", {"start": v(80, 69.54) * mm, "end": v(77, 69.54) * mm});
            skLineSegment(sketch, "E253.MirrorCS", {"start": v(77, 69.54) * mm, "end": v(77, 73.29) * mm});
            skLineSegment(sketch, "E254.MirrorCS", {"start": v(77, 77.04) * mm, "end": v(77, 73.29) * mm});
            skLineSegment(sketch, "E255.MirrorCS", {"start": v(80, 77.04) * mm, "end": v(77, 77.04) * mm});
            skLineSegment(sketch, "E256.MirrorCS", {"start": v(80, 86.97) * mm, "end": v(77, 86.97) * mm});
            skLineSegment(sketch, "E257.MirrorCS", {"start": v(77, 86.97) * mm, "end": v(77, 90.72) * mm});
            skLineSegment(sketch, "E258.MirrorCS", {"start": v(77, 94.47) * mm, "end": v(77, 90.72) * mm});
            skLineSegment(sketch, "E259.MirrorCS", {"start": v(80, 94.47) * mm, "end": v(77, 94.47) * mm});
            skCircle(sketch, "E260", {"center": v(40, 73.29) * mm, "radius": 25 * mm});
            skLineSegment(sketch, "E261", {"start": v(80, 104.4) * mm, "end": v(77, 104.4) * mm});
            skLineSegment(sketch, "E262", {"start": v(77, 104.4) * mm, "end": v(77, 108.16) * mm});
            skLineSegment(sketch, "E263.MirrorCS", {"start": v(0, 104.4) * mm, "end": v(3, 104.4) * mm});
            skLineSegment(sketch, "E264.MirrorCS", {"start": v(3, 104.4) * mm, "end": v(3, 108.16) * mm});
            skSolve(sketch);
        }
        {
            var Q0;
            Q0=qCreatedBy(id+"F6.planeOp",FACE);
            cPlane(context, id + "F20", {"entities" : qUnion([Q0]), "cplaneType" : CPlaneType.OFFSET, "offset" : (getVariable(context, 'HD')) * mm, "width" : 150 * mm, "height" : 150 * mm});
        }
        {
            var Q0;
            Q0=qCreatedBy(id+"F20.planeOp",FACE);
            var sketch = newSketch(context, id + "F21", { "sketchPlane" : qUnion([Q0])});
            skLineSegment(sketch, "E265.0", {"start": v(0, 0) * mm, "end": v(0, 240) * mm});
            skLineSegment(sketch, "E266.0", {"start": v(80, 240) * mm, "end": v(80, 0) * mm});
            skLineSegment(sketch, "E267.0", {"start": v(80, 240) * mm, "end": v(0, 240) * mm});
            skLineSegment(sketch, "E268.0", {"start": v(80, 0) * mm, "end": v(0, 0) * mm});
            skCircle(sketch, "E269.0", {"center": v(9, 9) * mm, "radius": 3 * mm});
            skCircle(sketch, "E270.0", {"center": v(71, 9) * mm, "radius": 3 * mm});
            skCircle(sketch, "E271.0", {"center": v(9, 231) * mm, "radius": 3 * mm});
            skCircle(sketch, "E272.0", {"center": v(71, 231) * mm, "radius": 3 * mm});
            skLineSegment(sketch, "E273", {"start": v(0, 160) * mm, "end": v(80, 160) * mm, "construction": true});
            skLineSegment(sketch, "E274", {"start": v(18, 160) * mm, "end": v(18, 240) * mm});
            skLineSegment(sketch, "E275", {"start": v(0, 80) * mm, "end": v(80, 80) * mm, "construction": true});
            skLineSegment(sketch, "E276", {"start": v(18, 80) * mm, "end": v(18, 0) * mm});
            skLineSegment(sketch, "E277.1.0.0", {"start": v(20, 80) * mm, "end": v(20, 0) * mm});
            skLineSegment(sketch, "E277.1.0.1", {"start": v(20, 160) * mm, "end": v(20, 240) * mm});
            skLineSegment(sketch, "E277.2.0.0", {"start": v(22, 80) * mm, "end": v(22, 0) * mm});
            skLineSegment(sketch, "E277.2.0.1", {"start": v(22, 160) * mm, "end": v(22, 240) * mm});
            skLineSegment(sketch, "E277.3.0.0", {"start": v(24, 80) * mm, "end": v(24, 0) * mm});
            skLineSegment(sketch, "E277.3.0.1", {"start": v(24, 160) * mm, "end": v(24, 240) * mm});
            skLineSegment(sketch, "E277.4.0.0", {"start": v(26, 80) * mm, "end": v(26, 0) * mm});
            skLineSegment(sketch, "E277.4.0.1", {"start": v(26, 160) * mm, "end": v(26, 240) * mm});
            skLineSegment(sketch, "E277.5.0.0", {"start": v(28, 80) * mm, "end": v(28, 0) * mm});
            skLineSegment(sketch, "E277.5.0.1", {"start": v(28, 160) * mm, "end": v(28, 240) * mm});
            skLineSegment(sketch, "E277.6.0.0", {"start": v(30, 80) * mm, "end": v(30, 0) * mm});
            skLineSegment(sketch, "E277.6.0.1", {"start": v(30, 160) * mm, "end": v(30, 240) * mm});
            skLineSegment(sketch, "E277.7.0.0", {"start": v(32, 80) * mm, "end": v(32, 0) * mm});
            skLineSegment(sketch, "E277.7.0.1", {"start": v(32, 160) * mm, "end": v(32, 240) * mm});
            skLineSegment(sketch, "E277.8.0.0", {"start": v(34, 80) * mm, "end": v(34, 0) * mm});
            skLineSegment(sketch, "E277.8.0.1", {"start": v(34, 160) * mm, "end": v(34, 240) * mm});
            skLineSegment(sketch, "E277.9.0.0", {"start": v(36, 80) * mm, "end": v(36, 0) * mm});
            skLineSegment(sketch, "E277.9.0.1", {"start": v(36, 160) * mm, "end": v(36, 240) * mm});
            skLineSegment(sketch, "E277.10.0.0", {"start": v(38, 80) * mm, "end": v(38, 0) * mm});
            skLineSegment(sketch, "E277.10.0.1", {"start": v(38, 160) * mm, "end": v(38, 240) * mm});
            skLineSegment(sketch, "E277.11.0.0", {"start": v(40, 80) * mm, "end": v(40, 0) * mm});
            skLineSegment(sketch, "E277.11.0.1", {"start": v(40, 160) * mm, "end": v(40, 240) * mm});
            skLineSegment(sketch, "E277.direction1", {"start": v(18, 0) * mm, "end": v(20, 0) * mm, "construction": true});
            skLineSegment(sketch, "E278", {"start": v(18, 160) * mm, "end": v(20, 160) * mm});
            skLineSegment(sketch, "E279", {"start": v(22, 160) * mm, "end": v(24, 160) * mm});
            skLineSegment(sketch, "E280", {"start": v(26, 160) * mm, "end": v(28, 160) * mm});
            skLineSegment(sketch, "E281", {"start": v(30, 160) * mm, "end": v(32, 160) * mm});
            skLineSegment(sketch, "E282", {"start": v(34, 160) * mm, "end": v(36, 160) * mm});
            skLineSegment(sketch, "E283", {"start": v(38, 160) * mm, "end": v(40, 160) * mm});
            skLineSegment(sketch, "E284", {"start": v(18, 80) * mm, "end": v(20, 80) * mm});
            skLineSegment(sketch, "E285", {"start": v(22, 80) * mm, "end": v(24, 80) * mm});
            skLineSegment(sketch, "E286", {"start": v(26, 80) * mm, "end": v(28, 80) * mm});
            skLineSegment(sketch, "E287", {"start": v(30, 80) * mm, "end": v(32, 80) * mm});
            skLineSegment(sketch, "E288", {"start": v(34, 80) * mm, "end": v(36, 80) * mm});
            skLineSegment(sketch, "E289", {"start": v(38, 80) * mm, "end": v(40, 80) * mm});
            skLineSegment(sketch, "E290", {"start": v(40, 240) * mm, "end": v(80, 160) * mm, "construction": true});
            skLineSegment(sketch, "E291", {"start": v(60, 240) * mm, "end": v(60, 160) * mm, "construction": true});
            skPoint(sketch, "E291.startSnap0", {"position": v(60, 200) * mm});
            skLineSegment(sketch, "E292", {"start": v(54, 240) * mm, "end": v(54, 160) * mm});
            skLineSegment(sketch, "E293.MirrorCS", {"start": v(66, 240) * mm, "end": v(66, 160) * mm});
            skLineSegment(sketch, "E294.MirrorCS", {"start": v(54, 0) * mm, "end": v(54, 80) * mm});
            skLineSegment(sketch, "E295.MirrorCS", {"start": v(66, 0) * mm, "end": v(66, 80) * mm});
            skLineSegment(sketch, "E296", {"start": v(54, 160) * mm, "end": v(66, 160) * mm});
            skLineSegment(sketch, "E297", {"start": v(54, 80) * mm, "end": v(66, 80) * mm});
            skPoint(sketch, "E298", {"position": v(18, 0) * mm});
            skPoint(sketch, "E299", {"position": v(20, 0) * mm});
            skSolve(sketch);
        }
        {
            var Q0;
            Q0=qCreatedBy(id+"F20.planeOp",FACE);
            var sketch = newSketch(context, id + "F22", { "sketchPlane" : qUnion([Q0])});
            skLineSegment(sketch, "E300.0", {"start": v(0, 0) * mm, "end": v(0, 240) * mm});
            skLineSegment(sketch, "E301.0", {"start": v(80, 240) * mm, "end": v(80, 0) * mm});
            skLineSegment(sketch, "E302.0", {"start": v(80, 240) * mm, "end": v(0, 240) * mm});
            skLineSegment(sketch, "E303.0", {"start": v(80, 0) * mm, "end": v(0, 0) * mm});
            skLineSegment(sketch, "E304.0", {"start": v(20, 160) * mm, "end": v(20, 240) * mm, "construction": true});
            skLineSegment(sketch, "E305.0", {"start": v(54, 240) * mm, "end": v(54, 160) * mm, "construction": true});
            skLineSegment(sketch, "E306.0", {"start": v(66, 240) * mm, "end": v(66, 160) * mm, "construction": true});
            skLineSegment(sketch, "E307.0", {"start": v(22, 160) * mm, "end": v(22, 240) * mm, "construction": true});
            skLineSegment(sketch, "E308.0", {"start": v(24, 160) * mm, "end": v(24, 240) * mm, "construction": true});
            skLineSegment(sketch, "E309.0", {"start": v(26, 160) * mm, "end": v(26, 240) * mm, "construction": true});
            skLineSegment(sketch, "E310.0", {"start": v(28, 160) * mm, "end": v(28, 240) * mm, "construction": true});
            skLineSegment(sketch, "E311.0", {"start": v(30, 160) * mm, "end": v(30, 240) * mm, "construction": true});
            skLineSegment(sketch, "E312.0", {"start": v(32, 160) * mm, "end": v(32, 240) * mm, "construction": true});
            skLineSegment(sketch, "E313.0", {"start": v(34, 160) * mm, "end": v(34, 240) * mm, "construction": true});
            skLineSegment(sketch, "E314.0", {"start": v(36, 160) * mm, "end": v(36, 240) * mm, "construction": true});
            skLineSegment(sketch, "E315.0", {"start": v(18, 160) * mm, "end": v(18, 240) * mm, "construction": true});
            skLineSegment(sketch, "E316.0", {"start": v(38, 160) * mm, "end": v(38, 240) * mm, "construction": true});
            skLineSegment(sketch, "E317.0", {"start": v(40, 160) * mm, "end": v(40, 240) * mm, "construction": true});
            skLineSegment(sketch, "E318", {"start": v(0, 192) * mm, "end": v(80, 192) * mm, "construction": true});
            skLineSegment(sketch, "E319", {"start": v(0, 48) * mm, "end": v(80, 48) * mm, "construction": true});
            skLineSegment(sketch, "E320", {"start": v(18, 192) * mm, "end": v(18, 48) * mm});
            skLineSegment(sketch, "E321.1.0.0", {"start": v(20, 192) * mm, "end": v(20, 48) * mm});
            skLineSegment(sketch, "E321.2.0.0", {"start": v(22, 192) * mm, "end": v(22, 48) * mm});
            skLineSegment(sketch, "E321.3.0.0", {"start": v(24, 192) * mm, "end": v(24, 48) * mm});
            skLineSegment(sketch, "E321.4.0.0", {"start": v(26, 192) * mm, "end": v(26, 48) * mm});
            skLineSegment(sketch, "E321.5.0.0", {"start": v(28, 192) * mm, "end": v(28, 48) * mm});
            skLineSegment(sketch, "E321.6.0.0", {"start": v(30, 192) * mm, "end": v(30, 48) * mm});
            skLineSegment(sketch, "E321.7.0.0", {"start": v(32, 192) * mm, "end": v(32, 48) * mm});
            skLineSegment(sketch, "E321.8.0.0", {"start": v(34, 192) * mm, "end": v(34, 48) * mm});
            skLineSegment(sketch, "E321.9.0.0", {"start": v(36, 192) * mm, "end": v(36, 48) * mm});
            skLineSegment(sketch, "E321.10.0.0", {"start": v(38, 192) * mm, "end": v(38, 48) * mm});
            skLineSegment(sketch, "E321.11.0.0", {"start": v(40, 192) * mm, "end": v(40, 48) * mm});
            skLineSegment(sketch, "E321.direction1", {"start": v(18, 48) * mm, "end": v(20, 48) * mm, "construction": true});
            skLineSegment(sketch, "E322", {"start": v(18, 192) * mm, "end": v(20, 192) * mm});
            skLineSegment(sketch, "E323", {"start": v(22, 192) * mm, "end": v(24, 192) * mm});
            skLineSegment(sketch, "E324", {"start": v(26, 192) * mm, "end": v(28, 192) * mm});
            skLineSegment(sketch, "E325", {"start": v(30, 192) * mm, "end": v(32, 192) * mm});
            skLineSegment(sketch, "E326", {"start": v(34, 192) * mm, "end": v(36, 192) * mm});
            skLineSegment(sketch, "E327", {"start": v(38, 192) * mm, "end": v(40, 192) * mm});
            skLineSegment(sketch, "E328", {"start": v(54, 192) * mm, "end": v(66, 192) * mm});
            skLineSegment(sketch, "E329", {"start": v(66, 192) * mm, "end": v(66, 48) * mm});
            skLineSegment(sketch, "E330", {"start": v(66, 48) * mm, "end": v(54, 48) * mm});
            skLineSegment(sketch, "E331", {"start": v(54, 48) * mm, "end": v(54, 192) * mm});
            skLineSegment(sketch, "E332", {"start": v(18, 48) * mm, "end": v(20, 48) * mm});
            skLineSegment(sketch, "E333", {"start": v(22, 48) * mm, "end": v(24, 48) * mm});
            skLineSegment(sketch, "E334", {"start": v(26, 48) * mm, "end": v(28, 48) * mm});
            skLineSegment(sketch, "E335", {"start": v(30, 48) * mm, "end": v(32, 48) * mm});
            skLineSegment(sketch, "E336", {"start": v(34, 48) * mm, "end": v(36, 48) * mm});
            skLineSegment(sketch, "E337", {"start": v(38, 48) * mm, "end": v(40, 48) * mm});
            skCircle(sketch, "E338.0", {"center": v(9, 231) * mm, "radius": 3 * mm});
            skCircle(sketch, "E339.0", {"center": v(71, 231) * mm, "radius": 3 * mm});
            skCircle(sketch, "E340.0", {"center": v(71, 9) * mm, "radius": 3 * mm});
            skCircle(sketch, "E341.0", {"center": v(9, 9) * mm, "radius": 3 * mm});
            skSolve(sketch);
        }
        {
            var Q0;
            Q0=qCreatedBy(id+"F20.planeOp",FACE);
            cPlane(context, id + "F23", {"entities" : qUnion([Q0]), "cplaneType" : CPlaneType.OFFSET, "offset" : (getVariable(context, 'WT')) * 2 * mm, "width" : 150 * mm, "height" : 150 * mm});
        }
        {
            var Q0;
            Q0=qCreatedBy(id+"F23.planeOp",FACE);
            var sketch = newSketch(context, id + "F24", { "sketchPlane" : qUnion([Q0])});
            skLineSegment(sketch, "E342.0", {"start": v(0, 0) * mm, "end": v(0, 240) * mm});
            skLineSegment(sketch, "E342.1", {"start": v(80, 240) * mm, "end": v(0, 240) * mm});
            skLineSegment(sketch, "E342.2", {"start": v(80, 240) * mm, "end": v(80, 0) * mm});
            skLineSegment(sketch, "E342.3", {"start": v(80, 0) * mm, "end": v(0, 0) * mm});
            skCircle(sketch, "E342.4", {"center": v(9, 231) * mm, "radius": 3 * mm});
            skCircle(sketch, "E342.5", {"center": v(71, 231) * mm, "radius": 3 * mm});
            skCircle(sketch, "E342.6", {"center": v(9, 9) * mm, "radius": 3 * mm});
            skCircle(sketch, "E342.7", {"center": v(71, 9) * mm, "radius": 3 * mm});
            skLineSegment(sketch, "E343.0.1.0", {"start": v(0, 240) * mm, "end": v(0, 480) * mm});
            skCircle(sketch, "E343.0.1.1", {"center": v(9, 249) * mm, "radius": 3 * mm});
            skCircle(sketch, "E343.0.1.2", {"center": v(71, 249) * mm, "radius": 3 * mm});
            skLineSegment(sketch, "E343.0.1.3", {"start": v(80, 480) * mm, "end": v(80, 240) * mm});
            skCircle(sketch, "E343.0.1.4", {"center": v(9, 471) * mm, "radius": 3 * mm});
            skCircle(sketch, "E343.0.1.5", {"center": v(71, 471) * mm, "radius": 3 * mm});
            skLineSegment(sketch, "E343.0.1.6", {"start": v(80, 480) * mm, "end": v(0, 480) * mm});
            skLineSegment(sketch, "E343.0.2.0", {"start": v(0, 480) * mm, "end": v(0, 720) * mm});
            skCircle(sketch, "E343.0.2.1", {"center": v(9, 489) * mm, "radius": 3 * mm});
            skCircle(sketch, "E343.0.2.2", {"center": v(71, 489) * mm, "radius": 3 * mm});
            skLineSegment(sketch, "E343.0.2.3", {"start": v(80, 720) * mm, "end": v(80, 480) * mm});
            skCircle(sketch, "E343.0.2.4", {"center": v(9, 711) * mm, "radius": 3 * mm});
            skCircle(sketch, "E343.0.2.5", {"center": v(71, 711) * mm, "radius": 3 * mm});
            skLineSegment(sketch, "E343.0.2.6", {"start": v(80, 720) * mm, "end": v(0, 720) * mm});
            skLineSegment(sketch, "E343.0.3.0", {"start": v(0, 720) * mm, "end": v(0, 960) * mm});
            skCircle(sketch, "E343.0.3.1", {"center": v(9, 729) * mm, "radius": 3 * mm});
            skCircle(sketch, "E343.0.3.2", {"center": v(71, 729) * mm, "radius": 3 * mm});
            skLineSegment(sketch, "E343.0.3.3", {"start": v(80, 960) * mm, "end": v(80, 720) * mm});
            skCircle(sketch, "E343.0.3.4", {"center": v(9, 951) * mm, "radius": 3 * mm});
            skCircle(sketch, "E343.0.3.5", {"center": v(71, 951) * mm, "radius": 3 * mm});
            skLineSegment(sketch, "E343.0.3.6", {"start": v(80, 960) * mm, "end": v(0, 960) * mm});
            skLineSegment(sketch, "E343.direction1", {"start": v(0, 0) * mm, "end": v(25, 0) * mm, "construction": true});
            skLineSegment(sketch, "E343.direction2", {"start": v(0, 0) * mm, "end": v(0, 240) * mm, "construction": true});
            skSolve(sketch);
        }
        {
            var Q0;
            Q0=qCreatedBy(id+"F8.planeOp",FACE);
            var sketch = newSketch(context, id + "F25", { "sketchPlane" : qUnion([Q0])});
            skLineSegment(sketch, "E344.0", {"start": v(-80, 80) * mm, "end": v(0, 80) * mm});
            skLineSegment(sketch, "E344.1", {"start": v(-80, 0) * mm, "end": v(-80, 80) * mm});
            skLineSegment(sketch, "E344.2", {"start": v(-80, 0) * mm, "end": v(0, 0) * mm});
            skLineSegment(sketch, "E345", {"start": v(0, 80) * mm, "end": v(9, 80) * mm});
            skLineSegment(sketch, "E346", {"start": v(9, 80) * mm, "end": v(9, 0) * mm});
            skLineSegment(sketch, "E347", {"start": v(9, 0) * mm, "end": v(0, 0) * mm});
            skCircle(sketch, "E348.0", {"center": v(-71, 71) * mm, "radius": 3 * mm});
            skCircle(sketch, "E349.0", {"center": v(-71, 9) * mm, "radius": 3 * mm});
            skCircle(sketch, "E350.0", {"center": v(-9, 40) * mm, "radius": 3 * mm});
            skLineSegment(sketch, "E351.0", {"start": v(-40, 65) * mm, "end": v(-73.25, 65) * mm});
            skLineSegment(sketch, "E351.1", {"start": v(-73.25, 15) * mm, "end": v(-73.25, 65) * mm});
            skLineSegment(sketch, "E351.2", {"start": v(-40, 15) * mm, "end": v(-73.25, 15) * mm});
            skLineSegment(sketch, "E351.3", {"start": v(-40, 15) * mm, "end": v(-40, 65) * mm});
            skLineSegment(sketch, "E352.0", {"start": v(3, 80) * mm, "end": v(3, 0) * mm, "construction": true});
            skLineSegment(sketch, "E353", {"start": v(3, 18) * mm, "end": v(0, 18) * mm});
            skLineSegment(sketch, "E354", {"start": v(0, 18) * mm, "end": v(0, 20) * mm});
            skLineSegment(sketch, "E355", {"start": v(0, 20) * mm, "end": v(3, 20) * mm});
            skLineSegment(sketch, "E356.0.1.0", {"start": v(0, 24) * mm, "end": v(3, 24) * mm});
            skLineSegment(sketch, "E356.0.1.1", {"start": v(0, 22) * mm, "end": v(0, 24) * mm});
            skLineSegment(sketch, "E356.0.1.2", {"start": v(3, 22) * mm, "end": v(0, 22) * mm});
            skLineSegment(sketch, "E356.0.2.0", {"start": v(0, 28) * mm, "end": v(3, 28) * mm});
            skLineSegment(sketch, "E356.0.2.1", {"start": v(0, 26) * mm, "end": v(0, 28) * mm});
            skLineSegment(sketch, "E356.0.2.2", {"start": v(3, 26) * mm, "end": v(0, 26) * mm});
            skLineSegment(sketch, "E356.0.3.0", {"start": v(0, 32) * mm, "end": v(3, 32) * mm});
            skLineSegment(sketch, "E356.0.3.1", {"start": v(0, 30) * mm, "end": v(0, 32) * mm});
            skLineSegment(sketch, "E356.0.3.2", {"start": v(3, 30) * mm, "end": v(0, 30) * mm});
            skLineSegment(sketch, "E356.0.4.0", {"start": v(0, 36) * mm, "end": v(3, 36) * mm});
            skLineSegment(sketch, "E356.0.4.1", {"start": v(0, 34) * mm, "end": v(0, 36) * mm});
            skLineSegment(sketch, "E356.0.4.2", {"start": v(3, 34) * mm, "end": v(0, 34) * mm});
            skLineSegment(sketch, "E356.0.5.0", {"start": v(0, 40) * mm, "end": v(3, 40) * mm});
            skLineSegment(sketch, "E356.0.5.1", {"start": v(0, 38) * mm, "end": v(0, 40) * mm});
            skLineSegment(sketch, "E356.0.5.2", {"start": v(3, 38) * mm, "end": v(0, 38) * mm});
            skLineSegment(sketch, "E356.direction1", {"start": v(0, 18) * mm, "end": v(25, 18) * mm, "construction": true});
            skLineSegment(sketch, "E356.direction2", {"start": v(0, 18) * mm, "end": v(0, 22) * mm, "construction": true});
            skLineSegment(sketch, "E357", {"start": v(-33.25, 77) * mm, "end": v(-33.25, 3) * mm});
            skLineSegment(sketch, "E358", {"start": v(-33.25, 65) * mm, "end": v(-40, 65) * mm, "construction": true});
            skLineSegment(sketch, "E359", {"start": v(-73.25, 65) * mm, "end": v(-80, 65) * mm, "construction": true});
            skLineSegment(sketch, "E360", {"start": v(-30.25, 3) * mm, "end": v(-30.25, 77) * mm});
            skLineSegment(sketch, "E361.0", {"start": v(-80, 77) * mm, "end": v(0, 77) * mm});
            skLineSegment(sketch, "E362.0", {"start": v(-80, 3) * mm, "end": v(0, 3) * mm});
            skLineSegment(sketch, "E363.0", {"start": v(-77, 80) * mm, "end": v(-77, 0) * mm});
            skLineSegment(sketch, "E364.0", {"start": v(-10, 80) * mm, "end": v(-10, 77) * mm});
            skLineSegment(sketch, "E364.1", {"start": v(-20, 80) * mm, "end": v(-20, 77) * mm});
            skLineSegment(sketch, "E364.2", {"start": v(-30, 80) * mm, "end": v(-30, 77) * mm});
            skLineSegment(sketch, "E364.3", {"start": v(-40, 80) * mm, "end": v(-40, 77) * mm});
            skLineSegment(sketch, "E364.4", {"start": v(-50, 80) * mm, "end": v(-50, 77) * mm});
            skLineSegment(sketch, "E364.5", {"start": v(-60, 80) * mm, "end": v(-60, 77) * mm});
            skLineSegment(sketch, "E364.6", {"start": v(-70, 80) * mm, "end": v(-70, 77) * mm});
            skLineSegment(sketch, "E365.0", {"start": v(-80, 71.1) * mm, "end": v(-77, 71.1) * mm});
            skLineSegment(sketch, "E365.1", {"start": v(-80, 62.34) * mm, "end": v(-77, 62.34) * mm});
            skLineSegment(sketch, "E365.2", {"start": v(-80, 53.6) * mm, "end": v(-77, 53.6) * mm});
            skLineSegment(sketch, "E365.3", {"start": v(-80, 44.84) * mm, "end": v(-77, 44.84) * mm});
            skLineSegment(sketch, "E365.4", {"start": v(-80, 36.1) * mm, "end": v(-77, 36.1) * mm});
            skLineSegment(sketch, "E365.5", {"start": v(-80, 27.34) * mm, "end": v(-77, 27.34) * mm});
            skLineSegment(sketch, "E365.6", {"start": v(-80, 18.6) * mm, "end": v(-77, 18.6) * mm});
            skLineSegment(sketch, "E366.0", {"start": v(-70, 0) * mm, "end": v(-70, 3) * mm});
            skLineSegment(sketch, "E367.0", {"start": v(-60, 0) * mm, "end": v(-60, 3) * mm});
            skLineSegment(sketch, "E367.1", {"start": v(-50, 0) * mm, "end": v(-50, 3) * mm});
            skLineSegment(sketch, "E367.2", {"start": v(-40, 0) * mm, "end": v(-40, 3) * mm});
            skLineSegment(sketch, "E367.3", {"start": v(-30, 0) * mm, "end": v(-30, 3) * mm});
            skLineSegment(sketch, "E367.4", {"start": v(-20, 0) * mm, "end": v(-20, 3) * mm});
            skLineSegment(sketch, "E367.5", {"start": v(-10, 0) * mm, "end": v(-10, 3) * mm});
            skLineSegment(sketch, "E368", {"start": v(0, 77) * mm, "end": v(9, 77) * mm});
            skLineSegment(sketch, "E369", {"start": v(6, 80) * mm, "end": v(6, 0) * mm});
            skLineSegment(sketch, "E370", {"start": v(0, 3) * mm, "end": v(9, 3) * mm});
            skLineSegment(sketch, "E371.0", {"start": v(0, 27.34) * mm, "end": v(-3, 27.34) * mm});
            skLineSegment(sketch, "E372.0", {"start": v(0, 18.6) * mm, "end": v(-3, 18.6) * mm});
            skLineSegment(sketch, "E373.0", {"start": v(0, 71.1) * mm, "end": v(-3, 71.1) * mm, "construction": true});
            skLineSegment(sketch, "E374", {"start": v(6, 71.1) * mm, "end": v(9, 71.1) * mm});
            skLineSegment(sketch, "E375", {"start": v(6, 62.34) * mm, "end": v(9, 62.34) * mm});
            skLineSegment(sketch, "E376", {"start": v(6, 53.6) * mm, "end": v(9, 53.6) * mm});
            skLineSegment(sketch, "E377", {"start": v(6, 44.84) * mm, "end": v(9, 44.84) * mm});
            skLineSegment(sketch, "E378", {"start": v(6, 27.34) * mm, "end": v(9, 27.34) * mm});
            skLineSegment(sketch, "E379", {"start": v(6, 18.6) * mm, "end": v(9, 18.6) * mm});
            skLineSegment(sketch, "E380", {"start": v(6, 36.1) * mm, "end": v(9, 36.1) * mm});
            skLineSegment(sketch, "E381.0", {"start": v(-80, 9.84) * mm, "end": v(-77, 9.84) * mm});
            skLineSegment(sketch, "E382", {"start": v(6, 9.84) * mm, "end": v(9, 9.76) * mm});
            skLineSegment(sketch, "E383", {"start": v(3, 40) * mm, "end": v(3, 38) * mm, "construction": true});
            skLineSegment(sketch, "E384", {"start": v(3, 36) * mm, "end": v(3, 34) * mm, "construction": true});
            skLineSegment(sketch, "E385", {"start": v(3, 32) * mm, "end": v(3, 30) * mm, "construction": true});
            skLineSegment(sketch, "E386", {"start": v(3, 32) * mm, "end": v(3, 30) * mm});
            skLineSegment(sketch, "E387", {"start": v(3, 28) * mm, "end": v(3, 26) * mm});
            skLineSegment(sketch, "E388", {"start": v(3, 26) * mm, "end": v(3, 24) * mm});
            skLineSegment(sketch, "E389", {"start": v(3, 22) * mm, "end": v(3, 20) * mm});
            skLineSegment(sketch, "E390", {"start": v(3, 40) * mm, "end": v(3, 38) * mm});
            skLineSegment(sketch, "E391", {"start": v(3, 36) * mm, "end": v(3, 34) * mm});
            skLineSegment(sketch, "E392", {"start": v(3, 18) * mm, "end": v(3, 20) * mm});
            skLineSegment(sketch, "E393", {"start": v(3, 24) * mm, "end": v(3, 22) * mm});
            skSolve(sketch);
        }
        {
            var Q0;
            Q0=qCreatedBy(id+"F8.planeOp",FACE);
            var sketch = newSketch(context, id + "F26", { "sketchPlane" : qUnion([Q0])});
            skLineSegment(sketch, "E394.0", {"start": v(-80, 80) * mm, "end": v(0, 80) * mm});
            skLineSegment(sketch, "E394.1", {"start": v(-80, 0) * mm, "end": v(-80, 80) * mm});
            skLineSegment(sketch, "E394.2", {"start": v(-80, 0) * mm, "end": v(0, 0) * mm});
            skLineSegment(sketch, "E394.3", {"start": v(9, 0) * mm, "end": v(0, 0) * mm});
            skLineSegment(sketch, "E394.4", {"start": v(9, 80) * mm, "end": v(9, 0) * mm});
            skLineSegment(sketch, "E394.5", {"start": v(0, 80) * mm, "end": v(9, 80) * mm});
            skCircle(sketch, "E395.0", {"center": v(-71, 71) * mm, "radius": 3 * mm});
            skLineSegment(sketch, "E395.1", {"start": v(-40, 65) * mm, "end": v(-73.25, 65) * mm});
            skLineSegment(sketch, "E395.2", {"start": v(-73.25, 15) * mm, "end": v(-73.25, 65) * mm});
            skLineSegment(sketch, "E395.3", {"start": v(-40, 15) * mm, "end": v(-73.25, 15) * mm});
            skLineSegment(sketch, "E395.4", {"start": v(-40, 15) * mm, "end": v(-40, 65) * mm});
            skCircle(sketch, "E395.5", {"center": v(-71, 9) * mm, "radius": 3 * mm});
            skCircle(sketch, "E396.0", {"center": v(-9, 40) * mm, "radius": 3 * mm});
            skLineSegment(sketch, "E397.0", {"start": v(0, 40) * mm, "end": v(3, 40) * mm});
            skLineSegment(sketch, "E397.1", {"start": v(0, 38) * mm, "end": v(0, 40) * mm});
            skLineSegment(sketch, "E397.2", {"start": v(0, 34) * mm, "end": v(0, 36) * mm});
            skLineSegment(sketch, "E397.3", {"start": v(0, 30) * mm, "end": v(0, 32) * mm});
            skLineSegment(sketch, "E397.4", {"start": v(0, 26) * mm, "end": v(0, 28) * mm});
            skLineSegment(sketch, "E397.5", {"start": v(0, 22) * mm, "end": v(0, 24) * mm});
            skLineSegment(sketch, "E397.6", {"start": v(0, 18) * mm, "end": v(0, 20) * mm});
            skLineSegment(sketch, "E397.7", {"start": v(0, 20) * mm, "end": v(3, 20) * mm});
            skLineSegment(sketch, "E397.8", {"start": v(3, 22) * mm, "end": v(0, 22) * mm});
            skLineSegment(sketch, "E397.9", {"start": v(0, 24) * mm, "end": v(3, 24) * mm});
            skLineSegment(sketch, "E397.10", {"start": v(3, 26) * mm, "end": v(0, 26) * mm});
            skLineSegment(sketch, "E397.11", {"start": v(0, 28) * mm, "end": v(3, 28) * mm});
            skLineSegment(sketch, "E397.12", {"start": v(3, 30) * mm, "end": v(0, 30) * mm});
            skLineSegment(sketch, "E397.13", {"start": v(0, 32) * mm, "end": v(3, 32) * mm});
            skLineSegment(sketch, "E397.14", {"start": v(3, 34) * mm, "end": v(0, 34) * mm});
            skLineSegment(sketch, "E397.15", {"start": v(0, 36) * mm, "end": v(3, 36) * mm});
            skLineSegment(sketch, "E397.16", {"start": v(3, 38) * mm, "end": v(0, 38) * mm});
            skLineSegment(sketch, "E397.17", {"start": v(3, 18) * mm, "end": v(0, 18) * mm});
            skLineSegment(sketch, "E398", {"start": v(3, 40) * mm, "end": v(3, 38) * mm});
            skLineSegment(sketch, "E399", {"start": v(3, 36) * mm, "end": v(3, 34) * mm});
            skLineSegment(sketch, "E400", {"start": v(3, 32) * mm, "end": v(3, 30) * mm});
            skLineSegment(sketch, "E401", {"start": v(3, 28) * mm, "end": v(3, 26) * mm});
            skLineSegment(sketch, "E402", {"start": v(3, 24) * mm, "end": v(3, 22) * mm});
            skLineSegment(sketch, "E403", {"start": v(3, 20) * mm, "end": v(3, 18) * mm});
            skSolve(sketch);
        }
        {
            var Q0;
            {var subQ0=sQuery(id+"F5.wireOp",EDGE,"E50");Q0=makeQuery(id+"F5.imprint","IMPRINT",FACE,{"disambiguationData":[TD([[makeQuery(id+"F5.imprint","IMPRINT",EDGE,{"derivedFrom":subQ0}),-1.0]])]});}
            var Q1;
            {var subQ0=sQuery(id+"F5.wireOp",EDGE,"E51.1.0.0");Q1=makeQuery(id+"F5.imprint","IMPRINT",FACE,{"disambiguationData":[TD([[makeQuery(id+"F5.imprint","IMPRINT",EDGE,{"derivedFrom":subQ0}),1.0]])]});}
            var Q2;
            {var subQ0=sQuery(id+"F5.wireOp",EDGE,"E51.3.0.0");Q2=makeQuery(id+"F5.imprint","IMPRINT",FACE,{"disambiguationData":[TD([[makeQuery(id+"F5.imprint","IMPRINT",EDGE,{"derivedFrom":subQ0}),1.0]])]});}
            var Q3;
            {var subQ0=sQuery(id+"F5.wireOp",EDGE,"E51.5.0.0");Q3=makeQuery(id+"F5.imprint","IMPRINT",FACE,{"disambiguationData":[TD([[makeQuery(id+"F5.imprint","IMPRINT",EDGE,{"derivedFrom":subQ0}),1.0]])]});}
            var Q4;
            {var subQ0=sQuery(id+"F5.wireOp",EDGE,"E47");var subQ1=sQuery(id+"F5.wireOp",EDGE,"E46");var subQ2=makeQuery(id+"F5.imprint","INTERSECT",VERTEX,{"derivedFrom":[subQ1,subQ0]});Q4=makeQuery(id+"F5.imprint","IMPRINT",FACE,{"disambiguationData":[TD([[makeQuery(id+"F5.imprint","IMPRINT",EDGE,{"disambiguationData":[TD([[subQ2,1.0]])],"derivedFrom":subQ1}),-1.0]])]});}
            var Q5;
            {var subQ3=sQuery(id+"F5.wireOp",EDGE,"E70.MirrorCS");Q5=makeQuery(id+"F5.imprint","IMPRINT",FACE,{"disambiguationData":[TD([[makeQuery(id+"F5.imprint","IMPRINT",EDGE,{"derivedFrom":subQ3}),-1.0]])]});}
            var Q6;
            {var subQ0=sQuery(id+"F5.wireOp",EDGE,"E68.MirrorCS");Q6=makeQuery(id+"F5.imprint","IMPRINT",FACE,{"disambiguationData":[TD([[makeQuery(id+"F5.imprint","IMPRINT",EDGE,{"derivedFrom":subQ0}),-1.0]])]});}
            var Q7;
            {var subQ0=sQuery(id+"F5.wireOp",EDGE,"E66.MirrorCS");Q7=makeQuery(id+"F5.imprint","IMPRINT",FACE,{"disambiguationData":[TD([[makeQuery(id+"F5.imprint","IMPRINT",EDGE,{"derivedFrom":subQ0}),-1.0]])]});}
            var Q8;
            {var subQ0=sQuery(id+"F5.wireOp",EDGE,"E64.MirrorCS");Q8=makeQuery(id+"F5.imprint","IMPRINT",FACE,{"disambiguationData":[TD([[makeQuery(id+"F5.imprint","IMPRINT",EDGE,{"derivedFrom":subQ0}),-1.0]])]});}
            var Q9;
            {var subQ0=sQuery(id+"F5.wireOp",EDGE,"E57.MirrorCS");Q9=makeQuery(id+"F5.imprint","IMPRINT",FACE,{"disambiguationData":[TD([[makeQuery(id+"F5.imprint","IMPRINT",EDGE,{"derivedFrom":subQ0}),-1.0]])]});}
            var Q10;
            {var subQ0=sQuery(id+"F5.wireOp",EDGE,"E55.MirrorCS");Q10=makeQuery(id+"F5.imprint","IMPRINT",FACE,{"disambiguationData":[TD([[makeQuery(id+"F5.imprint","IMPRINT",EDGE,{"derivedFrom":subQ0}),-1.0]])]});}
            var Q11;
            {var subQ0=sQuery(id+"F5.wireOp",EDGE,"E53.MirrorCS");Q11=makeQuery(id+"F5.imprint","IMPRINT",FACE,{"disambiguationData":[TD([[makeQuery(id+"F5.imprint","IMPRINT",EDGE,{"derivedFrom":subQ0}),-1.0]])]});}
            var Q12;
            {var subQ0=sQuery(id+"F5.wireOp",EDGE,"E61");Q12=makeQuery(id+"F5.imprint","IMPRINT",FACE,{"disambiguationData":[TD([[makeQuery(id+"F5.imprint","IMPRINT",EDGE,{"derivedFrom":subQ0}),-1.0]])]});}
            var Q13;
            {var subQ0=sQuery(id+"F5.wireOp",EDGE,"E62.0.2.0");Q13=makeQuery(id+"F5.imprint","IMPRINT",FACE,{"disambiguationData":[TD([[makeQuery(id+"F5.imprint","IMPRINT",EDGE,{"derivedFrom":subQ0}),-1.0]])]});}
            var Q14;
            {var subQ0=sQuery(id+"F5.wireOp",EDGE,"E62.0.4.0");Q14=makeQuery(id+"F5.imprint","IMPRINT",FACE,{"disambiguationData":[TD([[makeQuery(id+"F5.imprint","IMPRINT",EDGE,{"derivedFrom":subQ0}),-1.0]])]});}
            var Q15;
            {var subQ3=sQuery(id+"F5.wireOp",EDGE,"E62.0.6.0");Q15=makeQuery(id+"F5.imprint","IMPRINT",FACE,{"disambiguationData":[TD([[makeQuery(id+"F5.imprint","IMPRINT",EDGE,{"derivedFrom":subQ3}),-1.0]])]});}
            var Q16;
            {var subQ7=sQuery(id+"F5.wireOp",EDGE,"E49");var subQ21=makeQuery(id+"F5.imprint","INTERSECT",VERTEX,{"derivedFrom":[subQ7,sQuery(id+"F5.wireOp",EDGE,"E50")]});Q16=makeQuery(id+"F5.imprint","IMPRINT",FACE,{"disambiguationData":[TD([[makeQuery(id+"F5.imprint","IMPRINT",EDGE,{"disambiguationData":[TD([[subQ21,1.0]])],"derivedFrom":subQ7}),-1.0]])]});}
            var Q17;
            {var subQ3=sQuery(id+"F5.wireOp",EDGE,"E79.MirrorCS");Q17=makeQuery(id+"F5.imprint","IMPRINT",FACE,{"disambiguationData":[TD([[makeQuery(id+"F5.imprint","IMPRINT",EDGE,{"derivedFrom":subQ3}),1.0]])]});}
            var Q18;
            {var subQ0=sQuery(id+"F5.wireOp",EDGE,"E59.MirrorCS");Q18=makeQuery(id+"F5.imprint","IMPRINT",FACE,{"disambiguationData":[TD([[makeQuery(id+"F5.imprint","IMPRINT",EDGE,{"derivedFrom":subQ0}),-1.0]])]});}
            var Q19;
            {var subQ0=sQuery(id+"F5.wireOp",EDGE,"E45");var subQ1=sQuery(id+"F5.wireOp",EDGE,"E44.0");var subQ2=makeQuery(id+"F5.imprint","INTERSECT",VERTEX,{"derivedFrom":[subQ1,subQ0]});Q19=makeQuery(id+"F5.imprint","IMPRINT",FACE,{"disambiguationData":[TD([[makeQuery(id+"F5.imprint","IMPRINT",EDGE,{"disambiguationData":[TD([[subQ2,-1.0]])],"derivedFrom":subQ1}),1.0]])]});}
            var Q20;
            {var subQ0=sQuery(id+"F5.wireOp",EDGE,"E53.MirrorCS");Q20=makeQuery(id+"F5.imprint","IMPRINT",FACE,{"disambiguationData":[TD([[makeQuery(id+"F5.imprint","IMPRINT",EDGE,{"derivedFrom":subQ0}),1.0]])]});}
            extrude(context, id + "F27", {"entities" : qUnion([Q0, Q1, Q2, Q3, Q4, Q5, Q6, Q7, Q8, Q9, Q10, Q11, Q12, Q13, Q14, Q15, Q16, Q17, Q18, Q19, Q20]), "oppositeDirection" : true, "depth" : getVariable(context, 'WT') * mm});
        }
        {
            var Q0;
            {var subQ0=sQuery(id+"F7.wireOp",EDGE,"E84");var subQ9=sQuery(id+"F7.wireOp",EDGE,"E81.0");var subQ10=makeQuery(id+"F7.imprint","INTERSECT",VERTEX,{"derivedFrom":[subQ9,subQ0]});Q0=makeQuery(id+"F7.imprint","IMPRINT",FACE,{"disambiguationData":[TD([[makeQuery(id+"F7.imprint","IMPRINT",EDGE,{"disambiguationData":[TD([[subQ10,1.0]])],"derivedFrom":subQ9}),1.0]])]});}
            var Q1;
            {var subQ3=sQuery(id+"F7.wireOp",EDGE,"E85");Q1=makeQuery(id+"F7.imprint","IMPRINT",FACE,{"disambiguationData":[TD([[makeQuery(id+"F7.imprint","IMPRINT",EDGE,{"derivedFrom":subQ3}),1.0]])]});}
            var Q2;
            {var subQ0=sQuery(id+"F7.wireOp",EDGE,"E86.0.1.0");Q2=makeQuery(id+"F7.imprint","IMPRINT",FACE,{"disambiguationData":[TD([[makeQuery(id+"F7.imprint","IMPRINT",EDGE,{"derivedFrom":subQ0}),-1.0]])]});}
            var Q3;
            {var subQ0=sQuery(id+"F7.wireOp",EDGE,"E86.0.3.0");Q3=makeQuery(id+"F7.imprint","IMPRINT",FACE,{"disambiguationData":[TD([[makeQuery(id+"F7.imprint","IMPRINT",EDGE,{"derivedFrom":subQ0}),-1.0]])]});}
            var Q4;
            {var subQ0=sQuery(id+"F7.wireOp",EDGE,"E86.0.5.0");Q4=makeQuery(id+"F7.imprint","IMPRINT",FACE,{"disambiguationData":[TD([[makeQuery(id+"F7.imprint","IMPRINT",EDGE,{"derivedFrom":subQ0}),-1.0]])]});}
            var Q5;
            {var subQ3=sQuery(id+"F7.wireOp",EDGE,"E95.MirrorCS");Q5=makeQuery(id+"F7.imprint","IMPRINT",FACE,{"disambiguationData":[TD([[makeQuery(id+"F7.imprint","IMPRINT",EDGE,{"derivedFrom":subQ3}),1.0]])]});}
            var Q6;
            {var subQ0=sQuery(id+"F7.wireOp",EDGE,"E93.MirrorCS");Q6=makeQuery(id+"F7.imprint","IMPRINT",FACE,{"disambiguationData":[TD([[makeQuery(id+"F7.imprint","IMPRINT",EDGE,{"derivedFrom":subQ0}),1.0]])]});}
            var Q7;
            {var subQ0=sQuery(id+"F7.wireOp",EDGE,"E91.MirrorCS");Q7=makeQuery(id+"F7.imprint","IMPRINT",FACE,{"disambiguationData":[TD([[makeQuery(id+"F7.imprint","IMPRINT",EDGE,{"derivedFrom":subQ0}),1.0]])]});}
            var Q8;
            {var subQ0=sQuery(id+"F7.wireOp",EDGE,"E89.MirrorCS");Q8=makeQuery(id+"F7.imprint","IMPRINT",FACE,{"disambiguationData":[TD([[makeQuery(id+"F7.imprint","IMPRINT",EDGE,{"derivedFrom":subQ0}),1.0]])]});}
            extrude(context, id + "F28", {"entities" : qUnion([Q0, Q1, Q2, Q3, Q4, Q5, Q6, Q7, Q8]), "oppositeDirection" : true, "depth" : (getVariable(context, 'WT')) * mm});
        }
        {
            var Q0;
            Q0=makeQuery(id+"F3.imprint","IMPRINT",FACE,{"disambiguationData":[TD([[makeQuery(id+"F3.imprint","IMPRINT",EDGE,{"derivedFrom":sQuery(id+"F3.wireOp",EDGE,"E37.0")}),-1.0]])]});
            extrude(context, id + "F29", {"entities" : qUnion([Q0]), "oppositeDirection" : true, "depth" : (getVariable(context, 'WT')) * mm});
        }
        {
            var Q0;
            {var subQ3=sQuery(id+"F9.wireOp",EDGE,"E101.21");Q0=makeQuery(id+"F9.imprint","IMPRINT",FACE,{"disambiguationData":[TD([[makeQuery(id+"F9.imprint","IMPRINT",EDGE,{"derivedFrom":subQ3}),-1.0]])]});}
            var Q1;
            {var subQ0=sQuery(id+"F9.wireOp",EDGE,"E101.22");Q1=makeQuery(id+"F9.imprint","IMPRINT",FACE,{"disambiguationData":[TD([[makeQuery(id+"F9.imprint","IMPRINT",EDGE,{"derivedFrom":subQ0}),1.0]])]});}
            var Q2;
            {var subQ0=sQuery(id+"F9.wireOp",EDGE,"E101.24");Q2=makeQuery(id+"F9.imprint","IMPRINT",FACE,{"disambiguationData":[TD([[makeQuery(id+"F9.imprint","IMPRINT",EDGE,{"derivedFrom":subQ0}),1.0]])]});}
            var Q3;
            {var subQ0=sQuery(id+"F9.wireOp",EDGE,"E101.26");Q3=makeQuery(id+"F9.imprint","IMPRINT",FACE,{"disambiguationData":[TD([[makeQuery(id+"F9.imprint","IMPRINT",EDGE,{"derivedFrom":subQ0}),1.0]])]});}
            var Q4;
            {var subQ4=sQuery(id+"F9.wireOp",EDGE,"E101.4");var subQ23=makeQuery(id+"F9.imprint","INTERSECT",VERTEX,{"derivedFrom":[subQ4,sQuery(id+"F9.wireOp",EDGE,"E101.7")]});Q4=makeQuery(id+"F9.imprint","IMPRINT",FACE,{"disambiguationData":[TD([[makeQuery(id+"F9.imprint","IMPRINT",EDGE,{"disambiguationData":[TD([[subQ23,1.0]])],"derivedFrom":subQ4}),-1.0]])]});}
            var Q5;
            {var subQ3=sQuery(id+"F9.wireOp",EDGE,"E101.28");Q5=makeQuery(id+"F9.imprint","IMPRINT",FACE,{"disambiguationData":[TD([[makeQuery(id+"F9.imprint","IMPRINT",EDGE,{"derivedFrom":subQ3}),-1.0]])]});}
            var Q6;
            {var subQ0=sQuery(id+"F9.wireOp",EDGE,"E101.29");Q6=makeQuery(id+"F9.imprint","IMPRINT",FACE,{"disambiguationData":[TD([[makeQuery(id+"F9.imprint","IMPRINT",EDGE,{"derivedFrom":subQ0}),1.0]])]});}
            var Q7;
            {var subQ0=sQuery(id+"F9.wireOp",EDGE,"E101.18");Q7=makeQuery(id+"F9.imprint","IMPRINT",FACE,{"disambiguationData":[TD([[makeQuery(id+"F9.imprint","IMPRINT",EDGE,{"derivedFrom":subQ0}),1.0]])]});}
            var Q8;
            {var subQ0=sQuery(id+"F9.wireOp",EDGE,"E101.17");Q8=makeQuery(id+"F9.imprint","IMPRINT",FACE,{"disambiguationData":[TD([[makeQuery(id+"F9.imprint","IMPRINT",EDGE,{"derivedFrom":subQ0}),-1.0]])]});}
            var Q9;
            {var subQ0=sQuery(id+"F9.wireOp",EDGE,"E101.15");Q9=makeQuery(id+"F9.imprint","IMPRINT",FACE,{"disambiguationData":[TD([[makeQuery(id+"F9.imprint","IMPRINT",EDGE,{"derivedFrom":subQ0}),1.0]])]});}
            var Q10;
            {var subQ3=sQuery(id+"F9.wireOp",EDGE,"E101.14");Q10=makeQuery(id+"F9.imprint","IMPRINT",FACE,{"disambiguationData":[TD([[makeQuery(id+"F9.imprint","IMPRINT",EDGE,{"derivedFrom":subQ3}),-1.0]])]});}
            var Q11;
            {var subQ0=sQuery(id+"F9.wireOp",EDGE,"E101.3");var subQ1=sQuery(id+"F9.wireOp",EDGE,"E101.1");var subQ2=makeQuery(id+"F9.imprint","INTERSECT",VERTEX,{"derivedFrom":[subQ1,subQ0]});Q11=makeQuery(id+"F9.imprint","IMPRINT",FACE,{"disambiguationData":[TD([[makeQuery(id+"F9.imprint","IMPRINT",EDGE,{"disambiguationData":[TD([[subQ2,-1.0]])],"derivedFrom":subQ1}),-1.0]])]});}
            var Q12;
            {var subQ0=sQuery(id+"F9.wireOp",EDGE,"E101.12");Q12=makeQuery(id+"F9.imprint","IMPRINT",FACE,{"disambiguationData":[TD([[makeQuery(id+"F9.imprint","IMPRINT",EDGE,{"derivedFrom":subQ0}),1.0]])]});}
            var Q13;
            {var subQ0=sQuery(id+"F9.wireOp",EDGE,"E101.10");Q13=makeQuery(id+"F9.imprint","IMPRINT",FACE,{"disambiguationData":[TD([[makeQuery(id+"F9.imprint","IMPRINT",EDGE,{"derivedFrom":subQ0}),1.0]])]});}
            var Q14;
            {var subQ0=sQuery(id+"F9.wireOp",EDGE,"E101.8");Q14=makeQuery(id+"F9.imprint","IMPRINT",FACE,{"disambiguationData":[TD([[makeQuery(id+"F9.imprint","IMPRINT",EDGE,{"derivedFrom":subQ0}),1.0]])]});}
            var Q15;
            {var subQ3=sQuery(id+"F9.wireOp",EDGE,"E101.7");Q15=makeQuery(id+"F9.imprint","IMPRINT",FACE,{"disambiguationData":[TD([[makeQuery(id+"F9.imprint","IMPRINT",EDGE,{"derivedFrom":subQ3}),-1.0]])]});}
            var Q16;
            {var subQ0=sQuery(id+"F9.wireOp",EDGE,"E101.33");Q16=makeQuery(id+"F9.imprint","IMPRINT",FACE,{"disambiguationData":[TD([[makeQuery(id+"F9.imprint","IMPRINT",EDGE,{"derivedFrom":subQ0}),1.0]])]});}
            var Q17;
            {var subQ0=sQuery(id+"F9.wireOp",EDGE,"E101.31");Q17=makeQuery(id+"F9.imprint","IMPRINT",FACE,{"disambiguationData":[TD([[makeQuery(id+"F9.imprint","IMPRINT",EDGE,{"derivedFrom":subQ0}),1.0]])]});}
            var Q18;
            {var subQ0=sQuery(id+"F9.wireOp",EDGE,"E101.2");var subQ1=sQuery(id+"F9.wireOp",EDGE,"E101.0");var subQ2=makeQuery(id+"F9.imprint","INTERSECT",VERTEX,{"derivedFrom":[subQ1,subQ0]});Q18=makeQuery(id+"F9.imprint","IMPRINT",FACE,{"disambiguationData":[TD([[makeQuery(id+"F9.imprint","IMPRINT",EDGE,{"disambiguationData":[TD([[subQ2,-1.0]])],"derivedFrom":subQ1}),1.0]])]});}
            extrude(context, id + "F30", {"entities" : qUnion([Q0, Q1, Q2, Q3, Q4, Q5, Q6, Q7, Q8, Q9, Q10, Q11, Q12, Q13, Q14, Q15, Q16, Q17, Q18]), "depth" : (getVariable(context, 'WT')) * mm});
        }
        {
            var Q0;
            Q0=makeQuery(id+"F11.imprint","IMPRINT",FACE,{"disambiguationData":[TD([[makeQuery(id+"F11.imprint","IMPRINT",EDGE,{"derivedFrom":sQuery(id+"F11.wireOp",EDGE,"E117.0")}),1.0]])]});
            extrude(context, id + "F31", {"entities" : qUnion([Q0]), "oppositeDirection" : true, "depth" : (getVariable(context, 'WT')) * mm});
        }
        {
            var Q0;
            {var subQ4=sQuery(id+"F13.wireOp",EDGE,"E124.0");Q0=makeQuery(id+"F13.imprint","IMPRINT",FACE,{"disambiguationData":[TD([[makeQuery(id+"F13.imprint","IMPRINT",EDGE,{"derivedFrom":subQ4}),-1.0]])]});}
            extrude(context, id + "F32", {"entities" : qUnion([Q0]), "depth" : (getVariable(context, 'WT')) * mm});
        }
        {
            var Q0;
            {var subQ9=sQuery(id+"F15.wireOp",EDGE,"E156.0");Q0=makeQuery(id+"F15.imprint","IMPRINT",FACE,{"disambiguationData":[TD([[makeQuery(id+"F15.imprint","IMPRINT",EDGE,{"derivedFrom":subQ9}),1.0]])]});}
            extrude(context, id + "F33", {"entities" : qUnion([Q0]), "depth" : (getVariable(context, 'WT')) * mm});
        }
        {
            var Q0;
            {var subQ0=sQuery(id+"F5.wireOp",EDGE,"E64.MirrorCS");Q0=makeQuery(id+"F5.imprint","IMPRINT",FACE,{"disambiguationData":[TD([[makeQuery(id+"F5.imprint","IMPRINT",EDGE,{"derivedFrom":subQ0}),-1.0]])]});}
            var Q1;
            {var subQ0=sQuery(id+"F5.wireOp",EDGE,"E66.MirrorCS");Q1=makeQuery(id+"F5.imprint","IMPRINT",FACE,{"disambiguationData":[TD([[makeQuery(id+"F5.imprint","IMPRINT",EDGE,{"derivedFrom":subQ0}),-1.0]])]});}
            var Q2;
            {var subQ0=sQuery(id+"F5.wireOp",EDGE,"E68.MirrorCS");Q2=makeQuery(id+"F5.imprint","IMPRINT",FACE,{"disambiguationData":[TD([[makeQuery(id+"F5.imprint","IMPRINT",EDGE,{"derivedFrom":subQ0}),-1.0]])]});}
            var Q3;
            {var subQ3=sQuery(id+"F5.wireOp",EDGE,"E70.MirrorCS");Q3=makeQuery(id+"F5.imprint","IMPRINT",FACE,{"disambiguationData":[TD([[makeQuery(id+"F5.imprint","IMPRINT",EDGE,{"derivedFrom":subQ3}),-1.0]])]});}
            var Q4;
            {var subQ0=sQuery(id+"F5.wireOp",EDGE,"E47");var subQ1=sQuery(id+"F5.wireOp",EDGE,"E46");var subQ2=makeQuery(id+"F5.imprint","INTERSECT",VERTEX,{"derivedFrom":[subQ1,subQ0]});Q4=makeQuery(id+"F5.imprint","IMPRINT",FACE,{"disambiguationData":[TD([[makeQuery(id+"F5.imprint","IMPRINT",EDGE,{"disambiguationData":[TD([[subQ2,1.0]])],"derivedFrom":subQ1}),-1.0]])]});}
            var Q5;
            {var subQ0=sQuery(id+"F5.wireOp",EDGE,"E51.5.0.0");Q5=makeQuery(id+"F5.imprint","IMPRINT",FACE,{"disambiguationData":[TD([[makeQuery(id+"F5.imprint","IMPRINT",EDGE,{"derivedFrom":subQ0}),1.0]])]});}
            var Q6;
            {var subQ0=sQuery(id+"F5.wireOp",EDGE,"E51.3.0.0");Q6=makeQuery(id+"F5.imprint","IMPRINT",FACE,{"disambiguationData":[TD([[makeQuery(id+"F5.imprint","IMPRINT",EDGE,{"derivedFrom":subQ0}),1.0]])]});}
            var Q7;
            {var subQ0=sQuery(id+"F5.wireOp",EDGE,"E51.1.0.0");Q7=makeQuery(id+"F5.imprint","IMPRINT",FACE,{"disambiguationData":[TD([[makeQuery(id+"F5.imprint","IMPRINT",EDGE,{"derivedFrom":subQ0}),1.0]])]});}
            var Q8;
            {var subQ0=sQuery(id+"F5.wireOp",EDGE,"E50");Q8=makeQuery(id+"F5.imprint","IMPRINT",FACE,{"disambiguationData":[TD([[makeQuery(id+"F5.imprint","IMPRINT",EDGE,{"derivedFrom":subQ0}),-1.0]])]});}
            var Q9;
            {var subQ0=sQuery(id+"F5.wireOp",EDGE,"E61");Q9=makeQuery(id+"F5.imprint","IMPRINT",FACE,{"disambiguationData":[TD([[makeQuery(id+"F5.imprint","IMPRINT",EDGE,{"derivedFrom":subQ0}),-1.0]])]});}
            var Q10;
            {var subQ0=sQuery(id+"F5.wireOp",EDGE,"E62.0.2.0");Q10=makeQuery(id+"F5.imprint","IMPRINT",FACE,{"disambiguationData":[TD([[makeQuery(id+"F5.imprint","IMPRINT",EDGE,{"derivedFrom":subQ0}),-1.0]])]});}
            var Q11;
            {var subQ0=sQuery(id+"F5.wireOp",EDGE,"E62.0.4.0");Q11=makeQuery(id+"F5.imprint","IMPRINT",FACE,{"disambiguationData":[TD([[makeQuery(id+"F5.imprint","IMPRINT",EDGE,{"derivedFrom":subQ0}),-1.0]])]});}
            var Q12;
            {var subQ3=sQuery(id+"F5.wireOp",EDGE,"E62.0.6.0");Q12=makeQuery(id+"F5.imprint","IMPRINT",FACE,{"disambiguationData":[TD([[makeQuery(id+"F5.imprint","IMPRINT",EDGE,{"derivedFrom":subQ3}),-1.0]])]});}
            var Q13;
            {var subQ0=sQuery(id+"F5.wireOp",EDGE,"E45");var subQ1=sQuery(id+"F5.wireOp",EDGE,"E44.0");var subQ2=makeQuery(id+"F5.imprint","INTERSECT",VERTEX,{"derivedFrom":[subQ1,subQ0]});Q13=makeQuery(id+"F5.imprint","IMPRINT",FACE,{"disambiguationData":[TD([[makeQuery(id+"F5.imprint","IMPRINT",EDGE,{"disambiguationData":[TD([[subQ2,-1.0]])],"derivedFrom":subQ1}),1.0]])]});}
            var Q14;
            {var subQ0=sQuery(id+"F5.wireOp",EDGE,"E53.MirrorCS");Q14=makeQuery(id+"F5.imprint","IMPRINT",FACE,{"disambiguationData":[TD([[makeQuery(id+"F5.imprint","IMPRINT",EDGE,{"derivedFrom":subQ0}),-1.0]])]});}
            var Q15;
            {var subQ0=sQuery(id+"F5.wireOp",EDGE,"E55.MirrorCS");Q15=makeQuery(id+"F5.imprint","IMPRINT",FACE,{"disambiguationData":[TD([[makeQuery(id+"F5.imprint","IMPRINT",EDGE,{"derivedFrom":subQ0}),-1.0]])]});}
            var Q16;
            {var subQ0=sQuery(id+"F5.wireOp",EDGE,"E57.MirrorCS");Q16=makeQuery(id+"F5.imprint","IMPRINT",FACE,{"disambiguationData":[TD([[makeQuery(id+"F5.imprint","IMPRINT",EDGE,{"derivedFrom":subQ0}),-1.0]])]});}
            var Q17;
            {var subQ0=sQuery(id+"F5.wireOp",EDGE,"E59.MirrorCS");Q17=makeQuery(id+"F5.imprint","IMPRINT",FACE,{"disambiguationData":[TD([[makeQuery(id+"F5.imprint","IMPRINT",EDGE,{"derivedFrom":subQ0}),-1.0]])]});}
            var Q18;
            {var subQ0=sQuery(id+"F5.wireOp",EDGE,"E53.MirrorCS");Q18=makeQuery(id+"F5.imprint","IMPRINT",FACE,{"disambiguationData":[TD([[makeQuery(id+"F5.imprint","IMPRINT",EDGE,{"derivedFrom":subQ0}),1.0]])]});}
            var Q19;
            {var subQ3=sQuery(id+"F5.wireOp",EDGE,"E79.MirrorCS");Q19=makeQuery(id+"F5.imprint","IMPRINT",FACE,{"disambiguationData":[TD([[makeQuery(id+"F5.imprint","IMPRINT",EDGE,{"derivedFrom":subQ3}),1.0]])]});}
            extrude(context, id + "F34", {"entities" : qUnion([Q0, Q1, Q2, Q3, Q4, Q5, Q6, Q7, Q8, Q9, Q10, Q11, Q12, Q13, Q14, Q15, Q16, Q17, Q18, Q19]), "operationType" : NewBodyOperationType.REMOVE, "oppositeDirection" : true, "depth" : (getVariable(context, 'WT')) * mm});
        }
        {
            var Q0;
            {var subQ3=sQuery(id+"F7.wireOp",EDGE,"E85");Q0=makeQuery(id+"F7.imprint","IMPRINT",FACE,{"disambiguationData":[TD([[makeQuery(id+"F7.imprint","IMPRINT",EDGE,{"derivedFrom":subQ3}),1.0]])]});}
            var Q1;
            {var subQ0=sQuery(id+"F7.wireOp",EDGE,"E89.MirrorCS");Q1=makeQuery(id+"F7.imprint","IMPRINT",FACE,{"disambiguationData":[TD([[makeQuery(id+"F7.imprint","IMPRINT",EDGE,{"derivedFrom":subQ0}),1.0]])]});}
            var Q2;
            {var subQ0=sQuery(id+"F7.wireOp",EDGE,"E86.0.1.0");Q2=makeQuery(id+"F7.imprint","IMPRINT",FACE,{"disambiguationData":[TD([[makeQuery(id+"F7.imprint","IMPRINT",EDGE,{"derivedFrom":subQ0}),-1.0]])]});}
            var Q3;
            {var subQ0=sQuery(id+"F7.wireOp",EDGE,"E91.MirrorCS");Q3=makeQuery(id+"F7.imprint","IMPRINT",FACE,{"disambiguationData":[TD([[makeQuery(id+"F7.imprint","IMPRINT",EDGE,{"derivedFrom":subQ0}),1.0]])]});}
            var Q4;
            {var subQ0=sQuery(id+"F7.wireOp",EDGE,"E86.0.3.0");Q4=makeQuery(id+"F7.imprint","IMPRINT",FACE,{"disambiguationData":[TD([[makeQuery(id+"F7.imprint","IMPRINT",EDGE,{"derivedFrom":subQ0}),-1.0]])]});}
            var Q5;
            {var subQ0=sQuery(id+"F7.wireOp",EDGE,"E93.MirrorCS");Q5=makeQuery(id+"F7.imprint","IMPRINT",FACE,{"disambiguationData":[TD([[makeQuery(id+"F7.imprint","IMPRINT",EDGE,{"derivedFrom":subQ0}),1.0]])]});}
            var Q6;
            {var subQ0=sQuery(id+"F7.wireOp",EDGE,"E86.0.5.0");Q6=makeQuery(id+"F7.imprint","IMPRINT",FACE,{"disambiguationData":[TD([[makeQuery(id+"F7.imprint","IMPRINT",EDGE,{"derivedFrom":subQ0}),-1.0]])]});}
            var Q7;
            {var subQ3=sQuery(id+"F7.wireOp",EDGE,"E95.MirrorCS");Q7=makeQuery(id+"F7.imprint","IMPRINT",FACE,{"disambiguationData":[TD([[makeQuery(id+"F7.imprint","IMPRINT",EDGE,{"derivedFrom":subQ3}),1.0]])]});}
            extrude(context, id + "F35", {"entities" : qUnion([Q0, Q1, Q2, Q3, Q4, Q5, Q6, Q7]), "operationType" : NewBodyOperationType.REMOVE, "oppositeDirection" : true, "depth" : (getVariable(context, 'WT')) * mm});
        }
        {
            var Q0;
            {var subQ4=sQuery(id+"F13.wireOp",EDGE,"E124.0");Q0=makeQuery(id+"F13.imprint","IMPRINT",FACE,{"disambiguationData":[TD([[makeQuery(id+"F13.imprint","IMPRINT",EDGE,{"derivedFrom":subQ4}),-1.0]])]});}
            extrude(context, id + "F36", {"entities" : qUnion([Q0]), "operationType" : NewBodyOperationType.REMOVE, "depth" : (getVariable(context, 'WT')) * mm});
        }
        {
            var Q0;
            {var subQ9=sQuery(id+"F15.wireOp",EDGE,"E156.0");Q0=makeQuery(id+"F15.imprint","IMPRINT",FACE,{"disambiguationData":[TD([[makeQuery(id+"F15.imprint","IMPRINT",EDGE,{"derivedFrom":subQ9}),1.0]])]});}
            extrude(context, id + "F37", {"entities" : qUnion([Q0]), "operationType" : NewBodyOperationType.REMOVE, "depth" : (getVariable(context, 'WT')) * mm});
        }
        {
            var Q0;
            {var subQ3=sQuery(id+"F9.wireOp",EDGE,"E101.7");Q0=makeQuery(id+"F9.imprint","IMPRINT",FACE,{"disambiguationData":[TD([[makeQuery(id+"F9.imprint","IMPRINT",EDGE,{"derivedFrom":subQ3}),-1.0]])]});}
            var Q1;
            {var subQ0=sQuery(id+"F9.wireOp",EDGE,"E101.33");Q1=makeQuery(id+"F9.imprint","IMPRINT",FACE,{"disambiguationData":[TD([[makeQuery(id+"F9.imprint","IMPRINT",EDGE,{"derivedFrom":subQ0}),1.0]])]});}
            var Q2;
            {var subQ0=sQuery(id+"F9.wireOp",EDGE,"E101.8");Q2=makeQuery(id+"F9.imprint","IMPRINT",FACE,{"disambiguationData":[TD([[makeQuery(id+"F9.imprint","IMPRINT",EDGE,{"derivedFrom":subQ0}),1.0]])]});}
            var Q3;
            {var subQ0=sQuery(id+"F9.wireOp",EDGE,"E101.10");Q3=makeQuery(id+"F9.imprint","IMPRINT",FACE,{"disambiguationData":[TD([[makeQuery(id+"F9.imprint","IMPRINT",EDGE,{"derivedFrom":subQ0}),1.0]])]});}
            var Q4;
            {var subQ0=sQuery(id+"F9.wireOp",EDGE,"E101.12");Q4=makeQuery(id+"F9.imprint","IMPRINT",FACE,{"disambiguationData":[TD([[makeQuery(id+"F9.imprint","IMPRINT",EDGE,{"derivedFrom":subQ0}),1.0]])]});}
            var Q5;
            {var subQ0=sQuery(id+"F9.wireOp",EDGE,"E101.3");var subQ1=sQuery(id+"F9.wireOp",EDGE,"E101.1");var subQ2=makeQuery(id+"F9.imprint","INTERSECT",VERTEX,{"derivedFrom":[subQ1,subQ0]});Q5=makeQuery(id+"F9.imprint","IMPRINT",FACE,{"disambiguationData":[TD([[makeQuery(id+"F9.imprint","IMPRINT",EDGE,{"disambiguationData":[TD([[subQ2,-1.0]])],"derivedFrom":subQ1}),-1.0]])]});}
            var Q6;
            {var subQ3=sQuery(id+"F9.wireOp",EDGE,"E101.14");Q6=makeQuery(id+"F9.imprint","IMPRINT",FACE,{"disambiguationData":[TD([[makeQuery(id+"F9.imprint","IMPRINT",EDGE,{"derivedFrom":subQ3}),-1.0]])]});}
            var Q7;
            {var subQ0=sQuery(id+"F9.wireOp",EDGE,"E101.15");Q7=makeQuery(id+"F9.imprint","IMPRINT",FACE,{"disambiguationData":[TD([[makeQuery(id+"F9.imprint","IMPRINT",EDGE,{"derivedFrom":subQ0}),1.0]])]});}
            var Q8;
            {var subQ0=sQuery(id+"F9.wireOp",EDGE,"E101.17");Q8=makeQuery(id+"F9.imprint","IMPRINT",FACE,{"disambiguationData":[TD([[makeQuery(id+"F9.imprint","IMPRINT",EDGE,{"derivedFrom":subQ0}),-1.0]])]});}
            var Q9;
            {var subQ0=sQuery(id+"F9.wireOp",EDGE,"E101.18");Q9=makeQuery(id+"F9.imprint","IMPRINT",FACE,{"disambiguationData":[TD([[makeQuery(id+"F9.imprint","IMPRINT",EDGE,{"derivedFrom":subQ0}),1.0]])]});}
            var Q10;
            {var subQ3=sQuery(id+"F9.wireOp",EDGE,"E101.21");Q10=makeQuery(id+"F9.imprint","IMPRINT",FACE,{"disambiguationData":[TD([[makeQuery(id+"F9.imprint","IMPRINT",EDGE,{"derivedFrom":subQ3}),-1.0]])]});}
            var Q11;
            {var subQ0=sQuery(id+"F9.wireOp",EDGE,"E101.22");Q11=makeQuery(id+"F9.imprint","IMPRINT",FACE,{"disambiguationData":[TD([[makeQuery(id+"F9.imprint","IMPRINT",EDGE,{"derivedFrom":subQ0}),1.0]])]});}
            var Q12;
            {var subQ0=sQuery(id+"F9.wireOp",EDGE,"E101.24");Q12=makeQuery(id+"F9.imprint","IMPRINT",FACE,{"disambiguationData":[TD([[makeQuery(id+"F9.imprint","IMPRINT",EDGE,{"derivedFrom":subQ0}),1.0]])]});}
            var Q13;
            {var subQ0=sQuery(id+"F9.wireOp",EDGE,"E101.26");Q13=makeQuery(id+"F9.imprint","IMPRINT",FACE,{"disambiguationData":[TD([[makeQuery(id+"F9.imprint","IMPRINT",EDGE,{"derivedFrom":subQ0}),1.0]])]});}
            var Q14;
            {var subQ0=sQuery(id+"F9.wireOp",EDGE,"E101.2");var subQ1=sQuery(id+"F9.wireOp",EDGE,"E101.0");var subQ2=makeQuery(id+"F9.imprint","INTERSECT",VERTEX,{"derivedFrom":[subQ1,subQ0]});Q14=makeQuery(id+"F9.imprint","IMPRINT",FACE,{"disambiguationData":[TD([[makeQuery(id+"F9.imprint","IMPRINT",EDGE,{"disambiguationData":[TD([[subQ2,-1.0]])],"derivedFrom":subQ1}),1.0]])]});}
            var Q15;
            {var subQ3=sQuery(id+"F9.wireOp",EDGE,"E101.28");Q15=makeQuery(id+"F9.imprint","IMPRINT",FACE,{"disambiguationData":[TD([[makeQuery(id+"F9.imprint","IMPRINT",EDGE,{"derivedFrom":subQ3}),-1.0]])]});}
            var Q16;
            {var subQ0=sQuery(id+"F9.wireOp",EDGE,"E101.29");Q16=makeQuery(id+"F9.imprint","IMPRINT",FACE,{"disambiguationData":[TD([[makeQuery(id+"F9.imprint","IMPRINT",EDGE,{"derivedFrom":subQ0}),1.0]])]});}
            var Q17;
            {var subQ0=sQuery(id+"F9.wireOp",EDGE,"E101.31");Q17=makeQuery(id+"F9.imprint","IMPRINT",FACE,{"disambiguationData":[TD([[makeQuery(id+"F9.imprint","IMPRINT",EDGE,{"derivedFrom":subQ0}),1.0]])]});}
            extrude(context, id + "F38", {"entities" : qUnion([Q0, Q1, Q2, Q3, Q4, Q5, Q6, Q7, Q8, Q9, Q10, Q11, Q12, Q13, Q14, Q15, Q16, Q17]), "operationType" : NewBodyOperationType.REMOVE, "depth" : (getVariable(context, 'WT')) * mm});
        }
        {
            var Q0;
            {var subQ8=sQuery(id+"F17.wireOp",EDGE,"E193");Q0=makeQuery(id+"F17.imprint","IMPRINT",FACE,{"disambiguationData":[TD([[makeQuery(id+"F17.imprint","IMPRINT",EDGE,{"derivedFrom":subQ8}),1.0]])]});}
            extrude(context, id + "F39", {"entities" : qUnion([Q0]), "depth" : (getVariable(context, 'WT')) * mm});
        }
        {
            var Q0;
            {var subQ14=sQuery(id+"F17.wireOp",EDGE,"E193");Q0=makeQuery(id+"F17.imprint","IMPRINT",FACE,{"disambiguationData":[TD([[makeQuery(id+"F17.imprint","IMPRINT",EDGE,{"derivedFrom":subQ14}),1.0]])]});}
            extrude(context, id + "F40", {"entities" : qUnion([Q0]), "operationType" : NewBodyOperationType.REMOVE, "depth" : (getVariable(context, 'WT')) * mm});
        }
        {
            var Q0;
            {var subQ8=sQuery(id+"F19.wireOp",EDGE,"E229");Q0=makeQuery(id+"F19.imprint","IMPRINT",FACE,{"disambiguationData":[TD([[makeQuery(id+"F19.imprint","IMPRINT",EDGE,{"derivedFrom":subQ8}),1.0]])]});}
            extrude(context, id + "F41", {"entities" : qUnion([Q0]), "depth" : (getVariable(context, 'WT')) * mm});
        }
        {
            var Q0;
            {var subQ8=sQuery(id+"F19.wireOp",EDGE,"E229");Q0=makeQuery(id+"F19.imprint","IMPRINT",FACE,{"disambiguationData":[TD([[makeQuery(id+"F19.imprint","IMPRINT",EDGE,{"derivedFrom":subQ8}),1.0]])]});}
            extrude(context, id + "F42", {"entities" : qUnion([Q0]), "operationType" : NewBodyOperationType.REMOVE, "depth" : (getVariable(context, 'WT')) * mm});
        }
        {
            var Q0;
            {var subQ17=sQuery(id+"F21.wireOp",EDGE,"E265.0");Q0=makeQuery(id+"F21.imprint","IMPRINT",FACE,{"disambiguationData":[TD([[makeQuery(id+"F21.imprint","IMPRINT",EDGE,{"derivedFrom":subQ17}),-1.0]])]});}
            extrude(context, id + "F43", {"entities" : qUnion([Q0]), "oppositeDirection" : true, "depth" : (getVariable(context, 'WT')) * mm});
        }
        {
            var Q0;
            Q0=makeQuery(id+"F22.imprint","IMPRINT",FACE,{"disambiguationData":[TD([[makeQuery(id+"F22.imprint","IMPRINT",EDGE,{"derivedFrom":sQuery(id+"F22.wireOp",EDGE,"E300.0")}),-1.0]])]});
            extrude(context, id + "F44", {"entities" : qUnion([Q0]), "depth" : (getVariable(context, 'WT')) * mm});
        }
        {
            var Q0;
            Q0=makeQuery(id+"F24.imprint","IMPRINT",FACE,{"disambiguationData":[TD([[makeQuery(id+"F24.imprint","IMPRINT",EDGE,{"derivedFrom":sQuery(id+"F24.wireOp",EDGE,"E342.0")}),-1.0]])]});
            var Q1;
            Q1=makeQuery(id+"F24.imprint","IMPRINT",FACE,{"disambiguationData":[TD([[makeQuery(id+"F24.imprint","IMPRINT",EDGE,{"derivedFrom":sQuery(id+"F24.wireOp",EDGE,"E342.1")}),-1.0]])]});
            var Q2;
            Q2=makeQuery(id+"F24.imprint","IMPRINT",FACE,{"disambiguationData":[TD([[makeQuery(id+"F24.imprint","IMPRINT",EDGE,{"derivedFrom":sQuery(id+"F24.wireOp",EDGE,"E343.0.1.6")}),-1.0]])]});
            var Q3;
            Q3=makeQuery(id+"F24.imprint","IMPRINT",FACE,{"disambiguationData":[TD([[makeQuery(id+"F24.imprint","IMPRINT",EDGE,{"derivedFrom":sQuery(id+"F24.wireOp",EDGE,"E343.0.2.6")}),-1.0]])]});
            var Q4;
            Q4=makeQuery(id+"F24.imprint","IMPRINT",FACE,{"disambiguationData":[TD([[makeQuery(id+"F24.imprint","IMPRINT",EDGE,{"derivedFrom":sQuery(id+"F24.wireOp",EDGE,"E343.0.3.6")}),-1.0]])]});
            var Q5;
            Q5=makeQuery(id+"F24.imprint","IMPRINT",FACE,{"disambiguationData":[TD([[makeQuery(id+"F24.imprint","IMPRINT",EDGE,{"derivedFrom":sQuery(id+"F24.wireOp",EDGE,"E343.0.4.6")}),-1.0]])]});
            extrude(context, id + "F45", {"entities" : qUnion([Q0, Q1, Q2, Q3, Q4, Q5]), "oppositeDirection" : true, "depth" : (getVariable(context, 'WT')) * mm});
        }
        {
            var Q0;
            Q0=makeQuery(id+"F26.imprint","IMPRINT",FACE,{"disambiguationData":[TD([[makeQuery(id+"F26.imprint","IMPRINT",EDGE,{"derivedFrom":sQuery(id+"F26.wireOp",EDGE,"E394.0")}),-1.0]])]});
            extrude(context, id + "F46", {"entities" : qUnion([Q0]), "oppositeDirection" : true, "depth" : (getVariable(context, 'WT')) * mm});
        }
        {
            var Q0;
            Q0=makeQuery(id+"F3.imprint","IMPRINT",FACE,{"disambiguationData":[TD([[makeQuery(id+"F3.imprint","IMPRINT",EDGE,{"derivedFrom":sQuery(id+"F3.wireOp",EDGE,"E37.5")}),1.0]])]});
            extrude(context, id + "F47", {"entities" : qUnion([Q0]), "oppositeDirection" : true, "depth" : (getVariable(context, 'WT')) * mm});
        }
        {
            var Q0;
            {var subQ3=sQuery(id+"F25.wireOp",EDGE,"E364.6");Q0=makeQuery(id+"F25.imprint","IMPRINT",FACE,{"disambiguationData":[TD([[makeQuery(id+"F25.imprint","IMPRINT",EDGE,{"derivedFrom":subQ3}),-1.0]])]});}
            var Q1;
            {var subQ0=sQuery(id+"F25.wireOp",EDGE,"E365.0");Q1=makeQuery(id+"F25.imprint","IMPRINT",FACE,{"disambiguationData":[TD([[makeQuery(id+"F25.imprint","IMPRINT",EDGE,{"derivedFrom":subQ0}),-1.0]])]});}
            var Q2;
            {var subQ0=sQuery(id+"F25.wireOp",EDGE,"E365.2");Q2=makeQuery(id+"F25.imprint","IMPRINT",FACE,{"disambiguationData":[TD([[makeQuery(id+"F25.imprint","IMPRINT",EDGE,{"derivedFrom":subQ0}),-1.0]])]});}
            var Q3;
            {var subQ0=sQuery(id+"F25.wireOp",EDGE,"E365.4");Q3=makeQuery(id+"F25.imprint","IMPRINT",FACE,{"disambiguationData":[TD([[makeQuery(id+"F25.imprint","IMPRINT",EDGE,{"derivedFrom":subQ0}),-1.0]])]});}
            var Q4;
            {var subQ0=sQuery(id+"F25.wireOp",EDGE,"E365.6");Q4=makeQuery(id+"F25.imprint","IMPRINT",FACE,{"disambiguationData":[TD([[makeQuery(id+"F25.imprint","IMPRINT",EDGE,{"derivedFrom":subQ0}),-1.0]])]});}
            var Q5;
            {var subQ0=sQuery(id+"F25.wireOp",EDGE,"E344.2");var subQ1=sQuery(id+"F25.wireOp",EDGE,"E344.1");var subQ2=makeQuery(id+"F25.imprint","INTERSECT",VERTEX,{"derivedFrom":[subQ1,subQ0]});Q5=makeQuery(id+"F25.imprint","IMPRINT",FACE,{"disambiguationData":[TD([[makeQuery(id+"F25.imprint","IMPRINT",EDGE,{"disambiguationData":[TD([[subQ2,-1.0]])],"derivedFrom":subQ1}),-1.0]])]});}
            var Q6;
            {var subQ3=sQuery(id+"F25.wireOp",EDGE,"E366.0");Q6=makeQuery(id+"F25.imprint","IMPRINT",FACE,{"disambiguationData":[TD([[makeQuery(id+"F25.imprint","IMPRINT",EDGE,{"derivedFrom":subQ3}),1.0]])]});}
            var Q7;
            {var subQ0=sQuery(id+"F25.wireOp",EDGE,"E367.0");Q7=makeQuery(id+"F25.imprint","IMPRINT",FACE,{"disambiguationData":[TD([[makeQuery(id+"F25.imprint","IMPRINT",EDGE,{"derivedFrom":subQ0}),-1.0]])]});}
            var Q8;
            {var subQ3=sQuery(id+"F25.wireOp",EDGE,"E367.2");Q8=makeQuery(id+"F25.imprint","IMPRINT",FACE,{"disambiguationData":[TD([[makeQuery(id+"F25.imprint","IMPRINT",EDGE,{"derivedFrom":subQ3}),-1.0]])]});}
            var Q9;
            {var subQ0=sQuery(id+"F25.wireOp",EDGE,"E367.4");Q9=makeQuery(id+"F25.imprint","IMPRINT",FACE,{"disambiguationData":[TD([[makeQuery(id+"F25.imprint","IMPRINT",EDGE,{"derivedFrom":subQ0}),-1.0]])]});}
            var Q10;
            {var subQ0=sQuery(id+"F25.wireOp",EDGE,"E347");var subQ1=sQuery(id+"F25.wireOp",EDGE,"E346");var subQ2=makeQuery(id+"F25.imprint","INTERSECT",VERTEX,{"derivedFrom":[subQ1,subQ0]});Q10=makeQuery(id+"F25.imprint","IMPRINT",FACE,{"disambiguationData":[TD([[makeQuery(id+"F25.imprint","IMPRINT",EDGE,{"disambiguationData":[TD([[subQ2,1.0]])],"derivedFrom":subQ1}),-1.0]])]});}
            var Q11;
            {var subQ3=sQuery(id+"F25.wireOp",EDGE,"E382");Q11=makeQuery(id+"F25.imprint","IMPRINT",FACE,{"disambiguationData":[TD([[makeQuery(id+"F25.imprint","IMPRINT",EDGE,{"derivedFrom":subQ3}),-1.0]])]});}
            var Q12;
            {var subQ0=sQuery(id+"F25.wireOp",EDGE,"E378");Q12=makeQuery(id+"F25.imprint","IMPRINT",FACE,{"disambiguationData":[TD([[makeQuery(id+"F25.imprint","IMPRINT",EDGE,{"derivedFrom":subQ0}),-1.0]])]});}
            var Q13;
            {var subQ0=sQuery(id+"F25.wireOp",EDGE,"E377");Q13=makeQuery(id+"F25.imprint","IMPRINT",FACE,{"disambiguationData":[TD([[makeQuery(id+"F25.imprint","IMPRINT",EDGE,{"derivedFrom":subQ0}),-1.0]])]});}
            var Q14;
            {var subQ0=sQuery(id+"F25.wireOp",EDGE,"E375");Q14=makeQuery(id+"F25.imprint","IMPRINT",FACE,{"disambiguationData":[TD([[makeQuery(id+"F25.imprint","IMPRINT",EDGE,{"derivedFrom":subQ0}),-1.0]])]});}
            var Q15;
            {var subQ3=sQuery(id+"F25.wireOp",EDGE,"E374");Q15=makeQuery(id+"F25.imprint","IMPRINT",FACE,{"disambiguationData":[TD([[makeQuery(id+"F25.imprint","IMPRINT",EDGE,{"derivedFrom":subQ3}),1.0]])]});}
            var Q16;
            {var subQ0=sQuery(id+"F25.wireOp",EDGE,"E346");var subQ1=sQuery(id+"F25.wireOp",EDGE,"E345");var subQ2=makeQuery(id+"F25.imprint","INTERSECT",VERTEX,{"derivedFrom":[subQ1,subQ0]});Q16=makeQuery(id+"F25.imprint","IMPRINT",FACE,{"disambiguationData":[TD([[makeQuery(id+"F25.imprint","IMPRINT",EDGE,{"disambiguationData":[TD([[subQ2,1.0]])],"derivedFrom":subQ1}),-1.0]])]});}
            var Q17;
            {var subQ0=sQuery(id+"F25.wireOp",EDGE,"E364.0");Q17=makeQuery(id+"F25.imprint","IMPRINT",FACE,{"disambiguationData":[TD([[makeQuery(id+"F25.imprint","IMPRINT",EDGE,{"derivedFrom":subQ0}),-1.0]])]});}
            var Q18;
            {var subQ4=sQuery(id+"F25.wireOp",EDGE,"E364.2");Q18=makeQuery(id+"F25.imprint","IMPRINT",FACE,{"disambiguationData":[TD([[makeQuery(id+"F25.imprint","IMPRINT",EDGE,{"derivedFrom":subQ4}),-1.0]])]});}
            var Q19;
            {var subQ0=sQuery(id+"F25.wireOp",EDGE,"E364.4");Q19=makeQuery(id+"F25.imprint","IMPRINT",FACE,{"disambiguationData":[TD([[makeQuery(id+"F25.imprint","IMPRINT",EDGE,{"derivedFrom":subQ0}),-1.0]])]});}
            extrude(context, id + "F48", {"entities" : qUnion([Q0, Q1, Q2, Q3, Q4, Q5, Q6, Q7, Q8, Q9, Q10, Q11, Q12, Q13, Q14, Q15, Q16, Q17, Q18, Q19]), "operationType" : NewBodyOperationType.REMOVE, "oppositeDirection" : true, "depth" : (getVariable(context, 'WT')) * mm});
        }
        {
            var Q0;
            {var subQ0=sQuery(id+"F25.wireOp",EDGE,"E366.0");Q0=makeQuery(id+"F25.imprint","IMPRINT",FACE,{"disambiguationData":[TD([[makeQuery(id+"F25.imprint","IMPRINT",EDGE,{"derivedFrom":subQ0}),-1.0]])]});}
            var Q1;
            {var subQ0=sQuery(id+"F25.wireOp",EDGE,"E367.1");Q1=makeQuery(id+"F25.imprint","IMPRINT",FACE,{"disambiguationData":[TD([[makeQuery(id+"F25.imprint","IMPRINT",EDGE,{"derivedFrom":subQ0}),-1.0]])]});}
            var Q2;
            {var subQ0=sQuery(id+"F25.wireOp",EDGE,"E367.3");Q2=makeQuery(id+"F25.imprint","IMPRINT",FACE,{"disambiguationData":[TD([[makeQuery(id+"F25.imprint","IMPRINT",EDGE,{"derivedFrom":subQ0}),-1.0]])]});}
            var Q3;
            {var subQ0=sQuery(id+"F25.wireOp",EDGE,"E367.5");Q3=makeQuery(id+"F25.imprint","IMPRINT",FACE,{"disambiguationData":[TD([[makeQuery(id+"F25.imprint","IMPRINT",EDGE,{"derivedFrom":subQ0}),-1.0]])]});}
            var Q4;
            {var subQ0=sQuery(id+"F25.wireOp",EDGE,"E379");Q4=makeQuery(id+"F25.imprint","IMPRINT",FACE,{"disambiguationData":[TD([[makeQuery(id+"F25.imprint","IMPRINT",EDGE,{"derivedFrom":subQ0}),-1.0]])]});}
            var Q5;
            {var subQ0=sQuery(id+"F25.wireOp",EDGE,"E378");Q5=makeQuery(id+"F25.imprint","IMPRINT",FACE,{"disambiguationData":[TD([[makeQuery(id+"F25.imprint","IMPRINT",EDGE,{"derivedFrom":subQ0}),1.0]])]});}
            var Q6;
            {var subQ0=sQuery(id+"F25.wireOp",EDGE,"E376");Q6=makeQuery(id+"F25.imprint","IMPRINT",FACE,{"disambiguationData":[TD([[makeQuery(id+"F25.imprint","IMPRINT",EDGE,{"derivedFrom":subQ0}),-1.0]])]});}
            var Q7;
            {var subQ0=sQuery(id+"F25.wireOp",EDGE,"E374");Q7=makeQuery(id+"F25.imprint","IMPRINT",FACE,{"disambiguationData":[TD([[makeQuery(id+"F25.imprint","IMPRINT",EDGE,{"derivedFrom":subQ0}),-1.0]])]});}
            var Q8;
            {var subQ0=sQuery(id+"F25.wireOp",EDGE,"E364.0");Q8=makeQuery(id+"F25.imprint","IMPRINT",FACE,{"disambiguationData":[TD([[makeQuery(id+"F25.imprint","IMPRINT",EDGE,{"derivedFrom":subQ0}),1.0]])]});}
            var Q9;
            {var subQ0=sQuery(id+"F25.wireOp",EDGE,"E364.1");Q9=makeQuery(id+"F25.imprint","IMPRINT",FACE,{"disambiguationData":[TD([[makeQuery(id+"F25.imprint","IMPRINT",EDGE,{"derivedFrom":subQ0}),-1.0]])]});}
            var Q10;
            {var subQ0=sQuery(id+"F25.wireOp",EDGE,"E364.3");Q10=makeQuery(id+"F25.imprint","IMPRINT",FACE,{"disambiguationData":[TD([[makeQuery(id+"F25.imprint","IMPRINT",EDGE,{"derivedFrom":subQ0}),-1.0]])]});}
            var Q11;
            {var subQ0=sQuery(id+"F25.wireOp",EDGE,"E364.5");Q11=makeQuery(id+"F25.imprint","IMPRINT",FACE,{"disambiguationData":[TD([[makeQuery(id+"F25.imprint","IMPRINT",EDGE,{"derivedFrom":subQ0}),-1.0]])]});}
            var Q12;
            {var subQ3=sQuery(id+"F25.wireOp",EDGE,"E365.0");Q12=makeQuery(id+"F25.imprint","IMPRINT",FACE,{"disambiguationData":[TD([[makeQuery(id+"F25.imprint","IMPRINT",EDGE,{"derivedFrom":subQ3}),1.0]])]});}
            var Q13;
            {var subQ0=sQuery(id+"F25.wireOp",EDGE,"E365.1");Q13=makeQuery(id+"F25.imprint","IMPRINT",FACE,{"disambiguationData":[TD([[makeQuery(id+"F25.imprint","IMPRINT",EDGE,{"derivedFrom":subQ0}),-1.0]])]});}
            var Q14;
            {var subQ0=sQuery(id+"F25.wireOp",EDGE,"E365.3");Q14=makeQuery(id+"F25.imprint","IMPRINT",FACE,{"disambiguationData":[TD([[makeQuery(id+"F25.imprint","IMPRINT",EDGE,{"derivedFrom":subQ0}),-1.0]])]});}
            var Q15;
            {var subQ0=sQuery(id+"F25.wireOp",EDGE,"E365.5");Q15=makeQuery(id+"F25.imprint","IMPRINT",FACE,{"disambiguationData":[TD([[makeQuery(id+"F25.imprint","IMPRINT",EDGE,{"derivedFrom":subQ0}),-1.0]])]});}
            var Q16;
            {var subQ3=sQuery(id+"F25.wireOp",EDGE,"E381.0");Q16=makeQuery(id+"F25.imprint","IMPRINT",FACE,{"disambiguationData":[TD([[makeQuery(id+"F25.imprint","IMPRINT",EDGE,{"derivedFrom":subQ3}),-1.0]])]});}
            extrude(context, id + "F49", {"entities" : qUnion([Q0, Q1, Q2, Q3, Q4, Q5, Q6, Q7, Q8, Q9, Q10, Q11, Q12, Q13, Q14, Q15, Q16]), "operationType" : NewBodyOperationType.REMOVE, "oppositeDirection" : true, "depth" : (getVariable(context, 'WT')) * mm});
        }
    });
